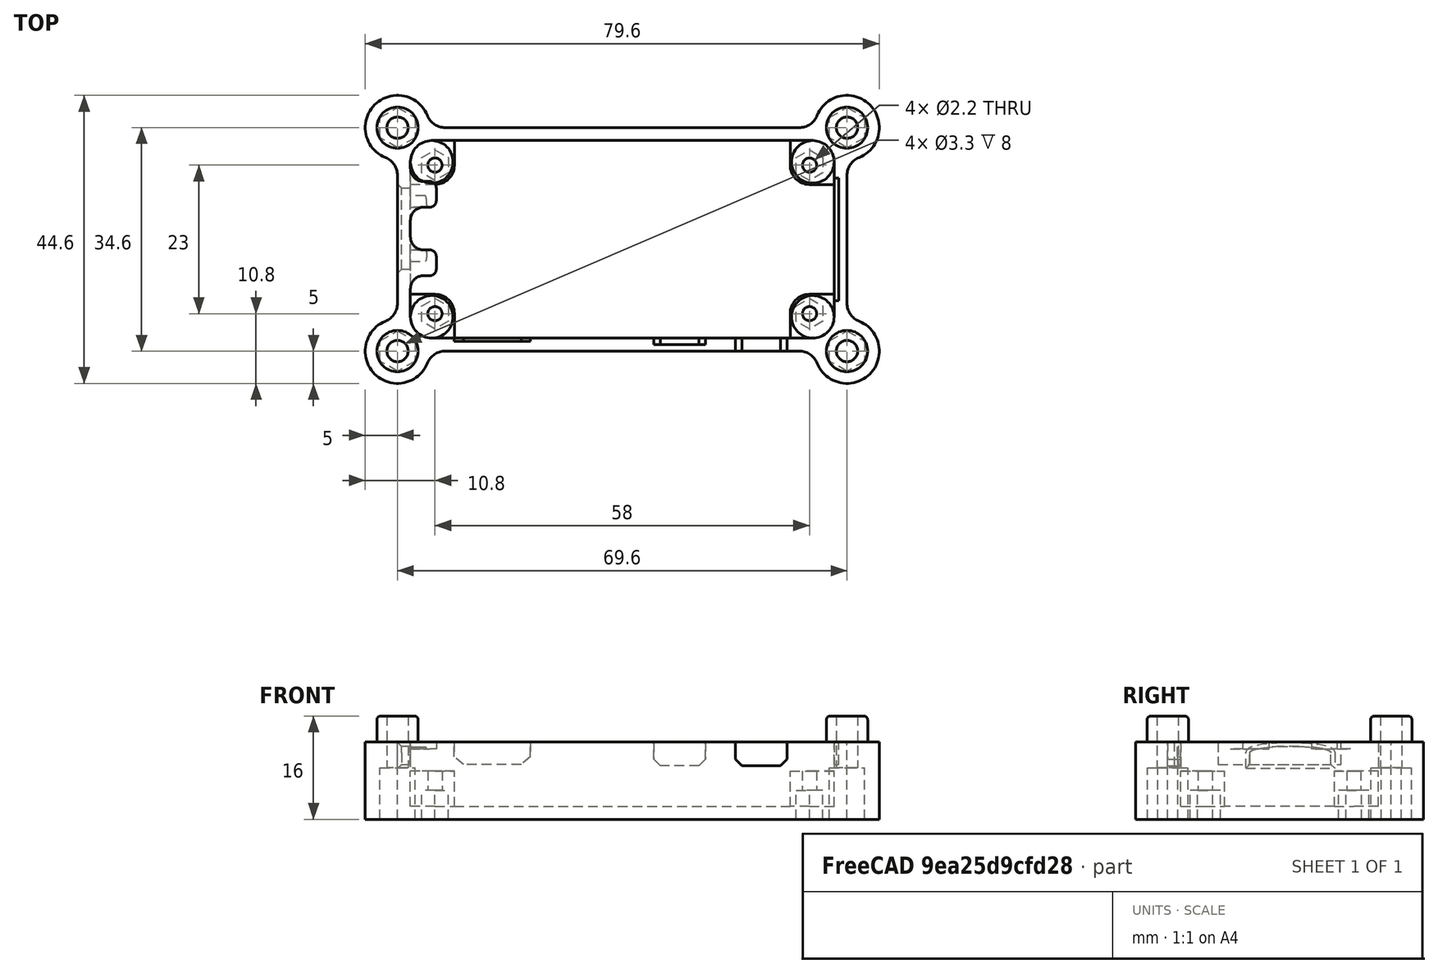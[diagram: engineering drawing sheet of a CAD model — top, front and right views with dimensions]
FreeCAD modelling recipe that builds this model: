
FCSTD DOCUMENT  (FreeCAD 0.18R14111 (Git))
Label: MMDVM_HS_Bottom-Single-USB
License: CreativeCommons Attribution-NonCommercial-ShareAlike
LicenseURL: http://creativecommons.org/licenses/by-nc-sa/4.0/
objects: Sketcher::SketchObject×16, PartDesign::Pocket×7, PartDesign::Pad×6, PartDesign::Fillet×5, PartDesign::Hole×2, PartDesign::Chamfer×1, PartDesign::Body×1, Mesh::Feature×1
note: 53 computed .brp shape members not serialized (recipe doc carries the construction recipe); baked Part::Feature solids carry a one-line shape summary decoded from their .brp

FEATURE [Sketcher::SketchObject] Sketch
  MapMode = 5
  Support = -> [XY_Plane]
  sketch-geometry (24):
    g0: LineSegment [constr] StartX=-32.5 StartY=15 StartZ=0 EndX=32.5 EndY=15 EndZ=0
    g1: LineSegment [constr] StartX=32.5 StartY=15 StartZ=0 EndX=32.5 EndY=-15 EndZ=0
    g2: LineSegment [constr] StartX=32.5 StartY=-15 StartZ=0 EndX=-32.5 EndY=-15 EndZ=0
    g3: LineSegment [constr] StartX=-32.5 StartY=-15 StartZ=0 EndX=-32.5 EndY=15 EndZ=0
    g4: LineSegment [constr] StartX=-29 StartY=11.5 StartZ=0 EndX=29 EndY=11.5 EndZ=0
    g5: LineSegment [constr] StartX=29 StartY=11.5 StartZ=0 EndX=29 EndY=-11.5 EndZ=0
    g6: LineSegment [constr] StartX=29 StartY=-11.5 StartZ=0 EndX=-29 EndY=-11.5 EndZ=0
    g7: LineSegment [constr] StartX=-29 StartY=-11.5 StartZ=0 EndX=-29 EndY=11.5 EndZ=0
    g8: Circle CenterX=-29 CenterY=11.5 CenterZ=0 NormalX=0 NormalY=0 NormalZ=1 AngleXU=0 Radius=1.375
    g9: Circle CenterX=29 CenterY=11.5 CenterZ=0 NormalX=0 NormalY=0 NormalZ=1 AngleXU=0 Radius=1.375
    g10: Circle CenterX=29 CenterY=-11.5 CenterZ=0 NormalX=0 NormalY=0 NormalZ=1 AngleXU=0 Radius=1.375
    g11: Circle CenterX=-29 CenterY=-11.5 CenterZ=0 NormalX=0 NormalY=0 NormalZ=1 AngleXU=0 Radius=1.375
    g12: LineSegment [constr] StartX=-29.5 StartY=12 StartZ=0 EndX=29.5 EndY=12 EndZ=0
    g13: LineSegment [constr] StartX=29.5 StartY=12 StartZ=0 EndX=29.5 EndY=-12 EndZ=0
    g14: LineSegment [constr] StartX=29.5 StartY=-12 StartZ=0 EndX=-29.5 EndY=-12 EndZ=0
    g15: LineSegment [constr] StartX=-29.5 StartY=-12 StartZ=0 EndX=-29.5 EndY=12 EndZ=0
    g16: ArcOfCircle CenterX=-29.5 CenterY=12 CenterZ=0 NormalX=0 NormalY=0 NormalZ=1 AngleXU=0 Radius=3 StartAngle=1.5708 EndAngle=3.1416
    g17: ArcOfCircle CenterX=29.5 CenterY=12 CenterZ=0 NormalX=0 NormalY=0 NormalZ=1 AngleXU=0 Radius=3 StartAngle=1.42077e-07 EndAngle=1.5708
    g18: ArcOfCircle CenterX=29.5 CenterY=-12 CenterZ=0 NormalX=0 NormalY=0 NormalZ=1 AngleXU=0 Radius=3 StartAngle=4.71239 EndAngle=6.28319
    g19: ArcOfCircle CenterX=-29.5 CenterY=-12 CenterZ=0 NormalX=0 NormalY=0 NormalZ=1 AngleXU=0 Radius=3 StartAngle=3.14159 EndAngle=4.71239
    g20: LineSegment StartX=-29.5 StartY=15 StartZ=0 EndX=29.5 EndY=15 EndZ=0
    g21: LineSegment StartX=32.5 StartY=12 StartZ=0 EndX=32.5 EndY=-12 EndZ=0
    g22: LineSegment StartX=29.5 StartY=-15 StartZ=0 EndX=-29.5 EndY=-15 EndZ=0
    g23: LineSegment StartX=-32.5 StartY=-12 StartZ=0 EndX=-32.5 EndY=12 EndZ=0
  constraints (68):
    c: Coincident(g0,g1)
    c: Coincident(g1,g2)
    c: Coincident(g2,g3)
    c: Coincident(g3,g0)
    c: Horizontal(g0)
    c: Horizontal(g2)
    c: Vertical(g1)
    c: Vertical(g3)
    c: DistanceX(g0,g0) = 65
    c: DistanceY(g1,g1) = 30
    c: Symmetric(g0,g0,g-2)
    c: Symmetric(g0,g1,g-1)
    c: Coincident(g4,g5)
    c: Coincident(g5,g6)
    c: Coincident(g6,g7)
    c: Coincident(g7,g4)
    c: Horizontal(g4)
    c: Horizontal(g6)
    c: Vertical(g5)
    c: Vertical(g7)
    c: DistanceX(g4,g4) = 58
    c: DistanceY(g5,g5) = 23
    c: Symmetric(g4,g5,g-1)
    c: Symmetric(g4,g4,g-2)
    c: Coincident(g8,g4)
    c: Coincident(g9,g4)
    c: Coincident(g10,g5)
    c: Coincident(g11,g6)
    c: Radius(g11) = 1.375
    c: Radius(g8) = 1.375
    c: Radius(g9) = 1.375
    c: Radius(g10) = 1.375
    c: Coincident(g12,g13)
    c: Coincident(g13,g14)
    c: Coincident(g14,g15)
    c: Coincident(g15,g12)
    c: Horizontal(g12)
    c: Horizontal(g14)
    c: Vertical(g13)
    c: Vertical(g15)
    c: DistanceX(g4,g12) = 0.5
    c: DistanceY(g4,g12) = 0.5
    c: DistanceY(g13,g5) = 0.5
    c: DistanceX(g14,g6) = 0.5
    c: Coincident(g16,g12)
    c: Radius(g16) = 3
    c: Coincident(g17,g12)
    c: Radius(g17) = 3
    c: Coincident(g18,g13)
    c: Radius(g18) = 3
    c: Coincident(g19,g14)
    c: Radius(g19) = 3
    c: PointOnObject(g16,g0)
    c: PointOnObject(g17,g1)
    c: PointOnObject(g18,g2)
    c: PointOnObject(g19,g3)
    c: Coincident(g20,g16)
    c: Horizontal(g20)
    c: Coincident(g20,g17)
    c: Coincident(g21,g17)
    c: Vertical(g21)
    c: Coincident(g18,g21)
    c: Coincident(g22,g18)
    c: Horizontal(g22)
    c: Coincident(g19,g22)
    c: Coincident(g23,g19)
    c: Vertical(g23)
    c: Coincident(g23,g16)
FEATURE [Sketcher::SketchObject] Sketch001
  MapMode = 5
  Support = -> [XY_Plane]
  expr: Constraints[8] = Sketch.Constraints[8]
  expr: Constraints[41] = Sketch.Constraints[41]
  expr: Constraints[9] = Sketch.Constraints[9]
  expr: Constraints[45] = Sketch.Constraints[45]
  expr: Constraints[43] = Sketch.Constraints[43]
  expr: Constraints[42] = Sketch.Constraints[42]
  expr: Constraints[20] = Sketch.Constraints[20]
  expr: Constraints[21] = Sketch.Constraints[21]
  expr: Constraints[28] = Sketch.Constraints[28]
  expr: Constraints[29] = Sketch.Constraints[29]
  expr: Constraints[30] = Sketch.Constraints[30]
  expr: Constraints[40] = Sketch.Constraints[40]
  expr: Constraints[31] = Sketch.Constraints[31]
  expr: Constraints[47] = Sketch.Constraints[47]
  expr: Constraints[49] = Sketch.Constraints[49]
  expr: Constraints[51] = Sketch.Constraints[51]
  sketch-geometry (64):
    g0: LineSegment [constr] StartX=-32.5 StartY=15 StartZ=0 EndX=32.5 EndY=15 EndZ=0
    g1: LineSegment [constr] StartX=32.5 StartY=15 StartZ=0 EndX=32.5 EndY=-15 EndZ=0
    g2: LineSegment [constr] StartX=32.5 StartY=-15 StartZ=0 EndX=-32.5 EndY=-15 EndZ=0
    g3: LineSegment [constr] StartX=-32.5 StartY=-15 StartZ=0 EndX=-32.5 EndY=15 EndZ=0
    g4: LineSegment [constr] StartX=-29 StartY=11.5 StartZ=0 EndX=29 EndY=11.5 EndZ=0
    g5: LineSegment [constr] StartX=29 StartY=11.5 StartZ=0 EndX=29 EndY=-11.5 EndZ=0
    g6: LineSegment [constr] StartX=29 StartY=-11.5 StartZ=0 EndX=-29 EndY=-11.5 EndZ=0
    g7: LineSegment [constr] StartX=-29 StartY=-11.5 StartZ=0 EndX=-29 EndY=11.5 EndZ=0
    g8: Circle [constr] CenterX=-29 CenterY=11.5 CenterZ=0 NormalX=0 NormalY=0 NormalZ=1 AngleXU=0 Radius=1.375
    g9: Circle [constr] CenterX=29 CenterY=11.5 CenterZ=0 NormalX=0 NormalY=0 NormalZ=1 AngleXU=0 Radius=1.375
    g10: Circle [constr] CenterX=29 CenterY=-11.5 CenterZ=0 NormalX=0 NormalY=0 NormalZ=1 AngleXU=0 Radius=1.375
    g11: Circle [constr] CenterX=-29 CenterY=-11.5 CenterZ=0 NormalX=0 NormalY=0 NormalZ=1 AngleXU=0 Radius=1.375
    g12: LineSegment [constr] StartX=-29.5 StartY=12 StartZ=0 EndX=29.5 EndY=12 EndZ=0
    g13: LineSegment [constr] StartX=29.5 StartY=12 StartZ=0 EndX=29.5 EndY=-12 EndZ=0
    g14: LineSegment [constr] StartX=29.5 StartY=-12 StartZ=0 EndX=-29.5 EndY=-12 EndZ=0
    g15: LineSegment [constr] StartX=-29.5 StartY=-12 StartZ=0 EndX=-29.5 EndY=12 EndZ=0
    g16: ArcOfCircle [constr] CenterX=-29.5 CenterY=12 CenterZ=0 NormalX=0 NormalY=0 NormalZ=1 AngleXU=0 Radius=3 StartAngle=1.5708 EndAngle=3.14159
    g17: ArcOfCircle [constr] CenterX=29.5 CenterY=12 CenterZ=0 NormalX=0 NormalY=0 NormalZ=1 AngleXU=0 Radius=3 StartAngle=2.8425e-08 EndAngle=1.5708
    g18: ArcOfCircle [constr] CenterX=29.5 CenterY=-12 CenterZ=0 NormalX=0 NormalY=0 NormalZ=1 AngleXU=0 Radius=3 StartAngle=4.71239 EndAngle=6.28319
    g19: ArcOfCircle [constr] CenterX=-29.5 CenterY=-12 CenterZ=0 NormalX=0 NormalY=0 NormalZ=1 AngleXU=0 Radius=3 StartAngle=3.14159 EndAngle=4.71239
    g20: LineSegment [constr] StartX=-29.5 StartY=15 StartZ=0 EndX=29.5 EndY=15 EndZ=0
    g21: LineSegment [constr] StartX=32.5 StartY=12 StartZ=0 EndX=32.5 EndY=-12 EndZ=0
    g22: LineSegment [constr] StartX=29.5 StartY=-15 StartZ=0 EndX=-29.5 EndY=-15 EndZ=0
    g23: LineSegment [constr] StartX=-32.5 StartY=-12 StartZ=0 EndX=-32.5 EndY=12 EndZ=0
    g24: ArcOfCircle [constr] CenterX=-29.5 CenterY=12 CenterZ=0 NormalX=0 NormalY=0 NormalZ=1 AngleXU=0 Radius=3.3 StartAngle=1.5708 EndAngle=3.14159
    g25: ArcOfCircle [constr] CenterX=29.5 CenterY=12 CenterZ=0 NormalX=0 NormalY=0 NormalZ=1 AngleXU=0 Radius=3.3 StartAngle=-2.2e-10 EndAngle=1.5708
    g26: ArcOfCircle [constr] CenterX=29.5 CenterY=-12 CenterZ=0 NormalX=0 NormalY=0 NormalZ=1 AngleXU=0 Radius=3.3 StartAngle=4.71239 EndAngle=6.28319
    g27: ArcOfCircle [constr] CenterX=-29.5 CenterY=-12 CenterZ=0 NormalX=0 NormalY=0 NormalZ=1 AngleXU=0 Radius=3.3 StartAngle=3.14159 EndAngle=4.71239
    g28: LineSegment [constr] StartX=-32.8 StartY=12 StartZ=0 EndX=-32.8 EndY=-12 EndZ=0
    g29: LineSegment [constr] StartX=-29.5 StartY=15.3 StartZ=0 EndX=29.5 EndY=15.3 EndZ=0
    g30: LineSegment [constr] StartX=32.8 StartY=12 StartZ=0 EndX=32.8 EndY=-12 EndZ=0
    g31: LineSegment [constr] StartX=29.5 StartY=-15.3 StartZ=0 EndX=-29.5 EndY=-15.3 EndZ=0
    g32: LineSegment [constr] StartX=-34.8 StartY=17.3 StartZ=0 EndX=34.8 EndY=17.3 EndZ=0
    g33: LineSegment [constr] StartX=34.8 StartY=17.3 StartZ=0 EndX=34.8 EndY=-17.3 EndZ=0
    g34: LineSegment [constr] StartX=34.8 StartY=-17.3 StartZ=0 EndX=-34.8 EndY=-17.3 EndZ=0
    g35: LineSegment [constr] StartX=-34.8 StartY=-17.3 StartZ=0 EndX=-34.8 EndY=17.3 EndZ=0
    g36: Circle [constr] CenterX=34.8 CenterY=17.3 CenterZ=0 NormalX=0 NormalY=0 NormalZ=1 AngleXU=0 Radius=5
    g37: Circle [constr] CenterX=34.8 CenterY=-17.3 CenterZ=0 NormalX=0 NormalY=0 NormalZ=1 AngleXU=0 Radius=5
    g38: Circle [constr] CenterX=-34.8 CenterY=-17.3 CenterZ=0 NormalX=0 NormalY=0 NormalZ=1 AngleXU=0 Radius=5
    g39: Circle [constr] CenterX=-34.8 CenterY=17.3 CenterZ=0 NormalX=0 NormalY=0 NormalZ=1 AngleXU=0 Radius=5
    g40: Circle [constr] CenterX=27.3838 CenterY=20.3 CenterZ=0 NormalX=0 NormalY=0 NormalZ=1 AngleXU=0 Radius=3
    g41: Circle [constr] CenterX=-27.3838 CenterY=20.3 CenterZ=0 NormalX=0 NormalY=0 NormalZ=1 AngleXU=0 Radius=3
    g42: Circle [constr] CenterX=-37.8 CenterY=9.8838 CenterZ=0 NormalX=0 NormalY=0 NormalZ=1 AngleXU=0 Radius=3
    g43: Circle [constr] CenterX=-37.8 CenterY=-9.8838 CenterZ=0 NormalX=0 NormalY=0 NormalZ=1 AngleXU=0 Radius=3
    g44: Circle [constr] CenterX=-27.3838 CenterY=-20.3 CenterZ=0 NormalX=0 NormalY=0 NormalZ=1 AngleXU=0 Radius=3
    g45: Circle [constr] CenterX=27.3838 CenterY=-20.3 CenterZ=0 NormalX=0 NormalY=0 NormalZ=1 AngleXU=0 Radius=3
    g46: Circle [constr] CenterX=37.8 CenterY=-9.8838 CenterZ=0 NormalX=0 NormalY=0 NormalZ=1 AngleXU=0 Radius=3
    g47: Circle [constr] CenterX=37.8 CenterY=9.8838 CenterZ=0 NormalX=0 NormalY=0 NormalZ=1 AngleXU=0 Radius=3
    g48: ArcOfCircle CenterX=34.8 CenterY=17.3 CenterZ=0 NormalX=0 NormalY=0 NormalZ=1 AngleXU=0 Radius=5 StartAngle=5.09679 EndAngle=9.04038
    g49: ArcOfCircle CenterX=27.3838 CenterY=20.3 CenterZ=0 NormalX=0 NormalY=0 NormalZ=1 AngleXU=0 Radius=3 StartAngle=4.71239 EndAngle=5.89879
    g50: ArcOfCircle CenterX=37.8 CenterY=9.8838 CenterZ=0 NormalX=0 NormalY=0 NormalZ=1 AngleXU=0 Radius=3 StartAngle=1.95519 EndAngle=3.14159
    g51: ArcOfCircle CenterX=37.8 CenterY=-9.8838 CenterZ=0 NormalX=0 NormalY=0 NormalZ=1 AngleXU=0 Radius=3 StartAngle=3.14159 EndAngle=4.32799
    g52: ArcOfCircle CenterX=34.8 CenterY=-17.3 CenterZ=0 NormalX=0 NormalY=0 NormalZ=1 AngleXU=0 Radius=5 StartAngle=3.52599 EndAngle=7.46958
    g53: ArcOfCircle CenterX=27.3838 CenterY=-20.3 CenterZ=0 NormalX=0 NormalY=0 NormalZ=1 AngleXU=0 Radius=3 StartAngle=0.384397 EndAngle=1.5708
    g54: ArcOfCircle CenterX=-27.3838 CenterY=-20.3 CenterZ=0 NormalX=0 NormalY=0 NormalZ=1 AngleXU=0 Radius=3 StartAngle=1.5708 EndAngle=2.7572
    g55: ArcOfCircle CenterX=-34.8 CenterY=-17.3 CenterZ=0 NormalX=0 NormalY=0 NormalZ=1 AngleXU=0 Radius=5 StartAngle=1.95519 EndAngle=5.89879
    g56: ArcOfCircle CenterX=-37.8 CenterY=-9.8838 CenterZ=0 NormalX=0 NormalY=0 NormalZ=1 AngleXU=0 Radius=3 StartAngle=5.09679 EndAngle=6.28319
    g57: ArcOfCircle CenterX=-37.8 CenterY=9.8838 CenterZ=0 NormalX=0 NormalY=0 NormalZ=1 AngleXU=0 Radius=3 StartAngle=6.28319 EndAngle=7.46958
    g58: ArcOfCircle CenterX=-34.8 CenterY=17.3 CenterZ=0 NormalX=0 NormalY=0 NormalZ=1 AngleXU=0 Radius=5 StartAngle=0.384397 EndAngle=4.32799
    g59: ArcOfCircle CenterX=-27.3838 CenterY=20.3 CenterZ=0 NormalX=0 NormalY=0 NormalZ=1 AngleXU=0 Radius=3 StartAngle=3.52599 EndAngle=4.71239
    g60: LineSegment StartX=-27.3838 StartY=17.3 StartZ=0 EndX=27.3838 EndY=17.3 EndZ=0
    g61: LineSegment StartX=34.8 StartY=9.8838 StartZ=0 EndX=34.8 EndY=-9.8838 EndZ=0
    g62: LineSegment StartX=27.3838 StartY=-17.3 StartZ=0 EndX=-27.3838 EndY=-17.3 EndZ=0
    g63: LineSegment StartX=-34.8 StartY=-9.8838 StartZ=0 EndX=-34.8 EndY=9.8838 EndZ=0
  constraints (184):
    c: Coincident(g0,g1)
    c: Coincident(g1,g2)
    c: Coincident(g2,g3)
    c: Coincident(g3,g0)
    c: Horizontal(g0)
    c: Horizontal(g2)
    c: Vertical(g1)
    c: Vertical(g3)
    c: DistanceX(g0,g0) = 65
    c: DistanceY(g1,g1) = 30
    c: Symmetric(g0,g0,g-2)
    c: Symmetric(g0,g1,g-1)
    c: Coincident(g4,g5)
    c: Coincident(g5,g6)
    c: Coincident(g6,g7)
    c: Coincident(g7,g4)
    c: Horizontal(g4)
    c: Horizontal(g6)
    c: Vertical(g5)
    c: Vertical(g7)
    c: DistanceX(g4,g4) = 58
    c: DistanceY(g5,g5) = 23
    c: Symmetric(g4,g5,g-1)
    c: Symmetric(g4,g4,g-2)
    c: Coincident(g8,g4)
    c: Coincident(g9,g4)
    c: Coincident(g10,g5)
    c: Coincident(g11,g6)
    c: Radius(g11) = 1.375
    c: Radius(g8) = 1.375
    c: Radius(g9) = 1.375
    c: Radius(g10) = 1.375
    c: Coincident(g12,g13)
    c: Coincident(g13,g14)
    c: Coincident(g14,g15)
    c: Coincident(g15,g12)
    c: Horizontal(g12)
    c: Horizontal(g14)
    c: Vertical(g13)
    c: Vertical(g15)
    c: DistanceX(g4,g12) = 0.5
    c: DistanceY(g4,g12) = 0.5
    c: DistanceY(g13,g5) = 0.5
    c: DistanceX(g14,g6) = 0.5
    c: Coincident(g16,g12)
    c: Radius(g16) = 3
    c: Coincident(g17,g12)
    c: Radius(g17) = 3
    c: Coincident(g18,g13)
    c: Radius(g18) = 3
    c: Coincident(g19,g14)
    c: Radius(g19) = 3
    c: PointOnObject(g16,g0)
    c: PointOnObject(g17,g1)
    c: PointOnObject(g18,g2)
    c: PointOnObject(g19,g3)
    c: Coincident(g20,g16)
    c: Horizontal(g20)
    c: Coincident(g20,g17)
    c: Coincident(g21,g17)
    c: Vertical(g21)
    c: Coincident(g18,g21)
    c: Coincident(g22,g18)
    c: Horizontal(g22)
    c: Coincident(g19,g22)
    c: Coincident(g23,g19)
    c: Vertical(g23)
    c: Coincident(g23,g16)
    c: Coincident(g24,g12)
    c: Radius(g24) = 3.3
    c: Coincident(g25,g12)
    c: Radius(g25) = 3.3
    c: Coincident(g26,g13)
    c: Radius(g26) = 3.3
    c: Coincident(g27,g14)
    c: Radius(g27) = 3.3
    c: Vertical(g28)
    c: DistanceX(g28,g2) = 0.3
    c: Coincident(g27,g28)
    c: Coincident(g28,g24)
    c: Horizontal(g29)
    c: DistanceY(g0,g29) = 0.3
    c: Coincident(g24,g29)
    c: Coincident(g25,g29)
    c: Vertical(g30)
    c: DistanceX(g0,g30) = 0.3
    c: Coincident(g25,g30)
    c: Coincident(g30,g26)
    c: Horizontal(g31)
    c: DistanceY(g31,g1) = 0.3
    c: Coincident(g31,g26)
    c: Coincident(g31,g27)
    c: Coincident(g32,g33)
    c: Coincident(g33,g34)
    c: Coincident(g34,g35)
    c: Coincident(g35,g32)
    c: Horizontal(g32)
    c: Horizontal(g34)
    c: Vertical(g33)
    c: Vertical(g35)
    c: DistanceY(g25,g32) = 2
    c: DistanceX(g25,g32) = 2
    c: DistanceY(g33,g26) = 2
    c: DistanceX(g34,g27) = 2
    c: Coincident(g36,g32)
    c: Coincident(g37,g33)
    c: Coincident(g38,g34)
    c: Coincident(g39,g32)
    c: Radius(g39) = 5
    c: Radius(g38) = 5
    c: Radius(g37) = 5
    c: Radius(g36) = 5
    c: Radius(g40) = 3
    c: Tangent(g40,g36)
    c: Tangent(g40,g32)
    c: Tangent(g47,g36)
    c: Radius(g47) = 3
    c: Tangent(g47,g33)
    c: Radius(g46) = 3
    c: Tangent(g46,g37)
    c: Tangent(g46,g33)
    c: Radius(g45) = 3
    c: Tangent(g45,g37)
    c: Tangent(g45,g34)
    c: Radius(g44) = 3
    c: Tangent(g44,g34)
    c: Tangent(g44,g38)
    c: Radius(g43) = 3
    c: Tangent(g43,g38)
    c: Tangent(g43,g35)
    c: Radius(g42) = 3
    c: Tangent(g42,g35)
    c: Tangent(g42,g39)
    c: Radius(g41) = 3
    c: Tangent(g41,g32)
    c: Tangent(g41,g39)
    c: Coincident(g48,g32)
    c: PointOnObject(g48,g36)
    c: Coincident(g49,g40)
    c: PointOnObject(g49,g40)
    c: Coincident(g50,g47)
    c: PointOnObject(g50,g47)
    c: Coincident(g51,g46)
    c: PointOnObject(g51,g46)
    c: Coincident(g52,g33)
    c: PointOnObject(g52,g37)
    c: Coincident(g53,g45)
    c: PointOnObject(g53,g45)
    c: Coincident(g54,g44)
    c: PointOnObject(g54,g44)
    c: Coincident(g55,g34)
    c: PointOnObject(g55,g38)
    c: Coincident(g56,g43)
    c: PointOnObject(g56,g43)
    c: Coincident(g57,g42)
    c: PointOnObject(g57,g42)
    c: Coincident(g58,g32)
    c: PointOnObject(g58,g39)
    c: Coincident(g59,g41)
    c: PointOnObject(g59,g41)
    c: Coincident(g49,g48)
    c: Coincident(g48,g50)
    c: Coincident(g51,g52)
    c: Coincident(g52,g53)
    c: Coincident(g54,g55)
    c: Coincident(g55,g56)
    c: Coincident(g57,g58)
    c: Coincident(g58,g59)
    c: PointOnObject(g60,g32)
    c: Horizontal(g60)
    c: PointOnObject(g61,g33)
    c: Vertical(g61)
    c: PointOnObject(g62,g34)
    c: Horizontal(g62)
    c: PointOnObject(g63,g35)
    c: Vertical(g63)
    c: Coincident(g59,g60)
    c: Coincident(g60,g49)
    c: Coincident(g50,g61)
    c: Coincident(g61,g51)
    c: Coincident(g53,g62)
    c: Coincident(g54,g62)
    c: Coincident(g56,g63)
    c: Coincident(g57,g63)
FEATURE [PartDesign::Pad] Pad
  Length = 12
  Length2 = 100
  Profile = -> Sketch001
  Type = 0
FEATURE [Sketcher::SketchObject] Sketch002
  MapMode = 5
  Placement = pos=(0,0,12) rot=(0,0,1;0rad)
  Support = -> [Pad]
  expr: Constraints[133] = Sketch001.Constraints[133]
  expr: Constraints[130] = Sketch001.Constraints[130]
  expr: Constraints[112] = Sketch001.Constraints[112]
  expr: Constraints[124] = Sketch001.Constraints[124]
  expr: Constraints[127] = Sketch001.Constraints[127]
  expr: Constraints[110] = Sketch001.Constraints[110]
  expr: Constraints[51] = Sketch001.Constraints[51]
  expr: Constraints[100] = Sketch001.Constraints[100]
  expr: Constraints[77] = Sketch001.Constraints[77]
  expr: Constraints[89] = Sketch001.Constraints[89]
  expr: Constraints[85] = Sketch001.Constraints[85]
  expr: Constraints[118] = Sketch001.Constraints[118]
  expr: Constraints[71] = Sketch001.Constraints[71]
  expr: Constraints[111] = Sketch001.Constraints[111]
  expr: Constraints[103] = Sketch001.Constraints[103]
  expr: Constraints[49] = Sketch001.Constraints[49]
  expr: Constraints[102] = Sketch001.Constraints[102]
  expr: Constraints[69] = Sketch001.Constraints[69]
  expr: Constraints[47] = Sketch001.Constraints[47]
  expr: Constraints[73] = Sketch001.Constraints[73]
  expr: Constraints[75] = Sketch001.Constraints[75]
  expr: Constraints[31] = Sketch001.Constraints[31]
  expr: Constraints[116] = Sketch001.Constraints[116]
  expr: Constraints[40] = Sketch001.Constraints[40]
  expr: Constraints[30] = Sketch001.Constraints[30]
  expr: Constraints[29] = Sketch001.Constraints[29]
  expr: Constraints[28] = Sketch001.Constraints[28]
  expr: Constraints[121] = Sketch001.Constraints[121]
  expr: Constraints[21] = Sketch001.Constraints[21]
  expr: Constraints[20] = Sketch001.Constraints[20]
  expr: Constraints[42] = Sketch001.Constraints[42]
  expr: Constraints[43] = Sketch001.Constraints[43]
  expr: Constraints[101] = Sketch001.Constraints[101]
  expr: Constraints[45] = Sketch001.Constraints[45]
  expr: Constraints[108] = Sketch001.Constraints[108]
  expr: Constraints[41] = Sketch001.Constraints[41]
  expr: Constraints[9] = Sketch001.Constraints[9]
  expr: Constraints[81] = Sketch001.Constraints[81]
  expr: Constraints[109] = Sketch001.Constraints[109]
  expr: Constraints[8] = Sketch001.Constraints[8]
  sketch-geometry (64):
    g0: LineSegment [constr] StartX=-32.5 StartY=15 StartZ=0 EndX=32.5 EndY=15 EndZ=0
    g1: LineSegment [constr] StartX=32.5 StartY=15 StartZ=0 EndX=32.5 EndY=-15 EndZ=0
    g2: LineSegment [constr] StartX=32.5 StartY=-15 StartZ=0 EndX=-32.5 EndY=-15 EndZ=0
    g3: LineSegment [constr] StartX=-32.5 StartY=-15 StartZ=0 EndX=-32.5 EndY=15 EndZ=0
    g4: LineSegment [constr] StartX=-29 StartY=11.5 StartZ=0 EndX=29 EndY=11.5 EndZ=0
    g5: LineSegment [constr] StartX=29 StartY=11.5 StartZ=0 EndX=29 EndY=-11.5 EndZ=0
    g6: LineSegment [constr] StartX=29 StartY=-11.5 StartZ=0 EndX=-29 EndY=-11.5 EndZ=0
    g7: LineSegment [constr] StartX=-29 StartY=-11.5 StartZ=0 EndX=-29 EndY=11.5 EndZ=0
    g8: Circle [constr] CenterX=-29 CenterY=11.5 CenterZ=0 NormalX=0 NormalY=0 NormalZ=1 AngleXU=0 Radius=1.375
    g9: Circle [constr] CenterX=29 CenterY=11.5 CenterZ=0 NormalX=0 NormalY=0 NormalZ=1 AngleXU=0 Radius=1.375
    g10: Circle [constr] CenterX=29 CenterY=-11.5 CenterZ=0 NormalX=0 NormalY=0 NormalZ=1 AngleXU=0 Radius=1.375
    g11: Circle [constr] CenterX=-29 CenterY=-11.5 CenterZ=0 NormalX=0 NormalY=0 NormalZ=1 AngleXU=0 Radius=1.375
    g12: LineSegment [constr] StartX=-29.5 StartY=12 StartZ=0 EndX=29.5 EndY=12 EndZ=0
    g13: LineSegment [constr] StartX=29.5 StartY=12 StartZ=0 EndX=29.5 EndY=-12 EndZ=0
    g14: LineSegment [constr] StartX=29.5 StartY=-12 StartZ=0 EndX=-29.5 EndY=-12 EndZ=0
    g15: LineSegment [constr] StartX=-29.5 StartY=-12 StartZ=0 EndX=-29.5 EndY=12 EndZ=0
    g16: ArcOfCircle [constr] CenterX=-29.5 CenterY=12 CenterZ=0 NormalX=0 NormalY=0 NormalZ=1 AngleXU=0 Radius=3 StartAngle=1.5708 EndAngle=3.14159
    g17: ArcOfCircle [constr] CenterX=29.5 CenterY=12 CenterZ=0 NormalX=0 NormalY=0 NormalZ=1 AngleXU=0 Radius=3 StartAngle=2.8425e-08 EndAngle=1.5708
    g18: ArcOfCircle [constr] CenterX=29.5 CenterY=-12 CenterZ=0 NormalX=0 NormalY=0 NormalZ=1 AngleXU=0 Radius=3 StartAngle=4.71239 EndAngle=6.28319
    g19: ArcOfCircle [constr] CenterX=-29.5 CenterY=-12 CenterZ=0 NormalX=0 NormalY=0 NormalZ=1 AngleXU=0 Radius=3 StartAngle=3.14159 EndAngle=4.71239
    g20: LineSegment [constr] StartX=-29.5 StartY=15 StartZ=0 EndX=29.5 EndY=15 EndZ=0
    g21: LineSegment [constr] StartX=32.5 StartY=12 StartZ=0 EndX=32.5 EndY=-12 EndZ=0
    g22: LineSegment [constr] StartX=29.5 StartY=-15 StartZ=0 EndX=-29.5 EndY=-15 EndZ=0
    g23: LineSegment [constr] StartX=-32.5 StartY=-12 StartZ=0 EndX=-32.5 EndY=12 EndZ=0
    g24: ArcOfCircle CenterX=-29.5 CenterY=12 CenterZ=0 NormalX=0 NormalY=0 NormalZ=1 AngleXU=0 Radius=3.3 StartAngle=1.5708 EndAngle=3.14159
    g25: ArcOfCircle CenterX=29.5 CenterY=12 CenterZ=0 NormalX=0 NormalY=0 NormalZ=1 AngleXU=0 Radius=3.3 StartAngle=-2.2e-10 EndAngle=1.5708
    g26: ArcOfCircle CenterX=29.5 CenterY=-12 CenterZ=0 NormalX=0 NormalY=0 NormalZ=1 AngleXU=0 Radius=3.3 StartAngle=4.71239 EndAngle=6.28319
    g27: ArcOfCircle CenterX=-29.5 CenterY=-12 CenterZ=0 NormalX=0 NormalY=0 NormalZ=1 AngleXU=0 Radius=3.3 StartAngle=3.14159 EndAngle=4.71239
    g28: LineSegment StartX=-32.8 StartY=12 StartZ=0 EndX=-32.8 EndY=-12 EndZ=0
    g29: LineSegment StartX=-29.5 StartY=15.3 StartZ=0 EndX=29.5 EndY=15.3 EndZ=0
    g30: LineSegment StartX=32.8 StartY=12 StartZ=0 EndX=32.8 EndY=-12 EndZ=0
    g31: LineSegment StartX=29.5 StartY=-15.3 StartZ=0 EndX=-29.5 EndY=-15.3 EndZ=0
    g32: LineSegment [constr] StartX=-34.8 StartY=17.3 StartZ=0 EndX=34.8 EndY=17.3 EndZ=0
    g33: LineSegment [constr] StartX=34.8 StartY=17.3 StartZ=0 EndX=34.8 EndY=-17.3 EndZ=0
    g34: LineSegment [constr] StartX=34.8 StartY=-17.3 StartZ=0 EndX=-34.8 EndY=-17.3 EndZ=0
    g35: LineSegment [constr] StartX=-34.8 StartY=-17.3 StartZ=0 EndX=-34.8 EndY=17.3 EndZ=0
    g36: Circle [constr] CenterX=34.8 CenterY=17.3 CenterZ=0 NormalX=0 NormalY=0 NormalZ=1 AngleXU=0 Radius=5
    g37: Circle [constr] CenterX=34.8 CenterY=-17.3 CenterZ=0 NormalX=0 NormalY=0 NormalZ=1 AngleXU=0 Radius=5
    g38: Circle [constr] CenterX=-34.8 CenterY=-17.3 CenterZ=0 NormalX=0 NormalY=0 NormalZ=1 AngleXU=0 Radius=5
    g39: Circle [constr] CenterX=-34.8 CenterY=17.3 CenterZ=0 NormalX=0 NormalY=0 NormalZ=1 AngleXU=0 Radius=5
    g40: Circle [constr] CenterX=27.3838 CenterY=20.3 CenterZ=0 NormalX=0 NormalY=0 NormalZ=1 AngleXU=0 Radius=3
    g41: Circle [constr] CenterX=-27.3838 CenterY=20.3 CenterZ=0 NormalX=0 NormalY=0 NormalZ=1 AngleXU=0 Radius=3
    g42: Circle [constr] CenterX=-37.8 CenterY=9.8838 CenterZ=0 NormalX=0 NormalY=0 NormalZ=1 AngleXU=0 Radius=3
    g43: Circle [constr] CenterX=-37.8 CenterY=-9.8838 CenterZ=0 NormalX=0 NormalY=0 NormalZ=1 AngleXU=0 Radius=3
    g44: Circle [constr] CenterX=-27.3838 CenterY=-20.3 CenterZ=0 NormalX=0 NormalY=0 NormalZ=1 AngleXU=0 Radius=3
    g45: Circle [constr] CenterX=27.3838 CenterY=-20.3 CenterZ=0 NormalX=0 NormalY=0 NormalZ=1 AngleXU=0 Radius=3
    g46: Circle [constr] CenterX=37.8 CenterY=-9.8838 CenterZ=0 NormalX=0 NormalY=0 NormalZ=1 AngleXU=0 Radius=3
    g47: Circle [constr] CenterX=37.8 CenterY=9.8838 CenterZ=0 NormalX=0 NormalY=0 NormalZ=1 AngleXU=0 Radius=3
    g48: ArcOfCircle [constr] CenterX=34.8 CenterY=17.3 CenterZ=0 NormalX=0 NormalY=0 NormalZ=1 AngleXU=0 Radius=5 StartAngle=5.09679 EndAngle=9.04038
    g49: ArcOfCircle [constr] CenterX=27.3838 CenterY=20.3 CenterZ=0 NormalX=0 NormalY=0 NormalZ=1 AngleXU=0 Radius=3 StartAngle=4.71239 EndAngle=5.89879
    g50: ArcOfCircle [constr] CenterX=37.8 CenterY=9.8838 CenterZ=0 NormalX=0 NormalY=0 NormalZ=1 AngleXU=0 Radius=3 StartAngle=1.95519 EndAngle=3.14159
    g51: ArcOfCircle [constr] CenterX=37.8 CenterY=-9.8838 CenterZ=0 NormalX=0 NormalY=0 NormalZ=1 AngleXU=0 Radius=3 StartAngle=3.14159 EndAngle=4.32799
    g52: ArcOfCircle [constr] CenterX=34.8 CenterY=-17.3 CenterZ=0 NormalX=0 NormalY=0 NormalZ=1 AngleXU=0 Radius=5 StartAngle=3.52599 EndAngle=7.46958
    g53: ArcOfCircle [constr] CenterX=27.3838 CenterY=-20.3 CenterZ=0 NormalX=0 NormalY=0 NormalZ=1 AngleXU=0 Radius=3 StartAngle=0.384397 EndAngle=1.5708
    g54: ArcOfCircle [constr] CenterX=-27.3838 CenterY=-20.3 CenterZ=0 NormalX=0 NormalY=0 NormalZ=1 AngleXU=0 Radius=3 StartAngle=1.5708 EndAngle=2.7572
    g55: ArcOfCircle [constr] CenterX=-34.8 CenterY=-17.3 CenterZ=0 NormalX=0 NormalY=0 NormalZ=1 AngleXU=0 Radius=5 StartAngle=1.95519 EndAngle=5.89879
    g56: ArcOfCircle [constr] CenterX=-37.8 CenterY=-9.8838 CenterZ=0 NormalX=0 NormalY=0 NormalZ=1 AngleXU=0 Radius=3 StartAngle=5.09679 EndAngle=6.28319
    g57: ArcOfCircle [constr] CenterX=-37.8 CenterY=9.8838 CenterZ=0 NormalX=0 NormalY=0 NormalZ=1 AngleXU=0 Radius=3 StartAngle=6.28319 EndAngle=7.46958
    g58: ArcOfCircle [constr] CenterX=-34.8 CenterY=17.3 CenterZ=0 NormalX=0 NormalY=0 NormalZ=1 AngleXU=0 Radius=5 StartAngle=0.384397 EndAngle=4.32799
    g59: ArcOfCircle [constr] CenterX=-27.3838 CenterY=20.3 CenterZ=0 NormalX=0 NormalY=0 NormalZ=1 AngleXU=0 Radius=3 StartAngle=3.52599 EndAngle=4.71239
    g60: LineSegment [constr] StartX=-27.3838 StartY=17.3 StartZ=0 EndX=27.3838 EndY=17.3 EndZ=0
    g61: LineSegment [constr] StartX=34.8 StartY=9.8838 StartZ=0 EndX=34.8 EndY=-9.8838 EndZ=0
    g62: LineSegment [constr] StartX=27.3838 StartY=-17.3 StartZ=0 EndX=-27.3838 EndY=-17.3 EndZ=0
    g63: LineSegment [constr] StartX=-34.8 StartY=-9.8838 StartZ=0 EndX=-34.8 EndY=9.8838 EndZ=0
  constraints (184):
    c: Coincident(g0,g1)
    c: Coincident(g1,g2)
    c: Coincident(g2,g3)
    c: Coincident(g3,g0)
    c: Horizontal(g0)
    c: Horizontal(g2)
    c: Vertical(g1)
    c: Vertical(g3)
    c: DistanceX(g0,g0) = 65
    c: DistanceY(g1,g1) = 30
    c: Symmetric(g0,g0,g-2)
    c: Symmetric(g0,g1,g-1)
    c: Coincident(g4,g5)
    c: Coincident(g5,g6)
    c: Coincident(g6,g7)
    c: Coincident(g7,g4)
    c: Horizontal(g4)
    c: Horizontal(g6)
    c: Vertical(g5)
    c: Vertical(g7)
    c: DistanceX(g4,g4) = 58
    c: DistanceY(g5,g5) = 23
    c: Symmetric(g4,g5,g-1)
    c: Symmetric(g4,g4,g-2)
    c: Coincident(g8,g4)
    c: Coincident(g9,g4)
    c: Coincident(g10,g5)
    c: Coincident(g11,g6)
    c: Radius(g11) = 1.375
    c: Radius(g8) = 1.375
    c: Radius(g9) = 1.375
    c: Radius(g10) = 1.375
    c: Coincident(g12,g13)
    c: Coincident(g13,g14)
    c: Coincident(g14,g15)
    c: Coincident(g15,g12)
    c: Horizontal(g12)
    c: Horizontal(g14)
    c: Vertical(g13)
    c: Vertical(g15)
    c: DistanceX(g4,g12) = 0.5
    c: DistanceY(g4,g12) = 0.5
    c: DistanceY(g13,g5) = 0.5
    c: DistanceX(g14,g6) = 0.5
    c: Coincident(g16,g12)
    c: Radius(g16) = 3
    c: Coincident(g17,g12)
    c: Radius(g17) = 3
    c: Coincident(g18,g13)
    c: Radius(g18) = 3
    c: Coincident(g19,g14)
    c: Radius(g19) = 3
    c: PointOnObject(g16,g0)
    c: PointOnObject(g17,g1)
    c: PointOnObject(g18,g2)
    c: PointOnObject(g19,g3)
    c: Coincident(g20,g16)
    c: Horizontal(g20)
    c: Coincident(g20,g17)
    c: Coincident(g21,g17)
    c: Vertical(g21)
    c: Coincident(g18,g21)
    c: Coincident(g22,g18)
    c: Horizontal(g22)
    c: Coincident(g19,g22)
    c: Coincident(g23,g19)
    c: Vertical(g23)
    c: Coincident(g23,g16)
    c: Coincident(g24,g12)
    c: Radius(g24) = 3.3
    c: Coincident(g25,g12)
    c: Radius(g25) = 3.3
    c: Coincident(g26,g13)
    c: Radius(g26) = 3.3
    c: Coincident(g27,g14)
    c: Radius(g27) = 3.3
    c: Vertical(g28)
    c: DistanceX(g28,g2) = 0.3
    c: Coincident(g27,g28)
    c: Coincident(g28,g24)
    c: Horizontal(g29)
    c: DistanceY(g0,g29) = 0.3
    c: Coincident(g24,g29)
    c: Coincident(g25,g29)
    c: Vertical(g30)
    c: DistanceX(g0,g30) = 0.3
    c: Coincident(g25,g30)
    c: Coincident(g30,g26)
    c: Horizontal(g31)
    c: DistanceY(g31,g1) = 0.3
    c: Coincident(g31,g26)
    c: Coincident(g31,g27)
    c: Coincident(g32,g33)
    c: Coincident(g33,g34)
    c: Coincident(g34,g35)
    c: Coincident(g35,g32)
    c: Horizontal(g32)
    c: Horizontal(g34)
    c: Vertical(g33)
    c: Vertical(g35)
    c: DistanceY(g25,g32) = 2
    c: DistanceX(g25,g32) = 2
    c: DistanceY(g33,g26) = 2
    c: DistanceX(g34,g27) = 2
    c: Coincident(g36,g32)
    c: Coincident(g37,g33)
    c: Coincident(g38,g34)
    c: Coincident(g39,g32)
    c: Radius(g39) = 5
    c: Radius(g38) = 5
    c: Radius(g37) = 5
    c: Radius(g36) = 5
    c: Radius(g40) = 3
    c: Tangent(g40,g36)
    c: Tangent(g40,g32)
    c: Tangent(g47,g36)
    c: Radius(g47) = 3
    c: Tangent(g47,g33)
    c: Radius(g46) = 3
    c: Tangent(g46,g37)
    c: Tangent(g46,g33)
    c: Radius(g45) = 3
    c: Tangent(g45,g37)
    c: Tangent(g45,g34)
    c: Radius(g44) = 3
    c: Tangent(g44,g34)
    c: Tangent(g44,g38)
    c: Radius(g43) = 3
    c: Tangent(g43,g38)
    c: Tangent(g43,g35)
    c: Radius(g42) = 3
    c: Tangent(g42,g35)
    c: Tangent(g42,g39)
    c: Radius(g41) = 3
    c: Tangent(g41,g32)
    c: Tangent(g41,g39)
    c: Coincident(g48,g32)
    c: PointOnObject(g48,g36)
    c: Coincident(g49,g40)
    c: PointOnObject(g49,g40)
    c: Coincident(g50,g47)
    c: PointOnObject(g50,g47)
    c: Coincident(g51,g46)
    c: PointOnObject(g51,g46)
    c: Coincident(g52,g33)
    c: PointOnObject(g52,g37)
    c: Coincident(g53,g45)
    c: PointOnObject(g53,g45)
    c: Coincident(g54,g44)
    c: PointOnObject(g54,g44)
    c: Coincident(g55,g34)
    c: PointOnObject(g55,g38)
    c: Coincident(g56,g43)
    c: PointOnObject(g56,g43)
    c: Coincident(g57,g42)
    c: PointOnObject(g57,g42)
    c: Coincident(g58,g32)
    c: PointOnObject(g58,g39)
    c: Coincident(g59,g41)
    c: PointOnObject(g59,g41)
    c: Coincident(g49,g48)
    c: Coincident(g48,g50)
    c: Coincident(g51,g52)
    c: Coincident(g52,g53)
    c: Coincident(g54,g55)
    c: Coincident(g55,g56)
    c: Coincident(g57,g58)
    c: Coincident(g58,g59)
    c: PointOnObject(g60,g32)
    c: Horizontal(g60)
    c: PointOnObject(g61,g33)
    c: Vertical(g61)
    c: PointOnObject(g62,g34)
    c: Horizontal(g62)
    c: PointOnObject(g63,g35)
    c: Vertical(g63)
    c: Coincident(g59,g60)
    c: Coincident(g60,g49)
    c: Coincident(g50,g61)
    c: Coincident(g61,g51)
    c: Coincident(g53,g62)
    c: Coincident(g54,g62)
    c: Coincident(g56,g63)
    c: Coincident(g57,g63)
FEATURE [PartDesign::Pocket] Pocket
  BaseFeature = -> Pad
  Length = 10
  Length2 = 100
  Profile = -> Sketch002
  Type = 0
FEATURE [Sketcher::SketchObject] Sketch003
  MapMode = 5
  Placement = pos=(0,0,2) rot=(0,0,1;0rad)
  Support = -> [Pocket]
  expr: Constraints[133] = Sketch002.Constraints[133]
  expr: Constraints[130] = Sketch002.Constraints[130]
  expr: Constraints[112] = Sketch002.Constraints[112]
  expr: Constraints[127] = Sketch002.Constraints[127]
  expr: Constraints[124] = Sketch002.Constraints[124]
  expr: Constraints[110] = Sketch002.Constraints[110]
  expr: Constraints[51] = Sketch002.Constraints[51]
  expr: Constraints[100] = Sketch002.Constraints[100]
  expr: Constraints[77] = Sketch002.Constraints[77]
  expr: Constraints[89] = Sketch002.Constraints[89]
  expr: Constraints[85] = Sketch002.Constraints[85]
  expr: Constraints[118] = Sketch002.Constraints[118]
  expr: Constraints[111] = Sketch002.Constraints[111]
  expr: Constraints[103] = Sketch002.Constraints[103]
  expr: Constraints[71] = Sketch002.Constraints[71]
  expr: Constraints[102] = Sketch002.Constraints[102]
  expr: Constraints[49] = Sketch002.Constraints[49]
  expr: Constraints[69] = Sketch002.Constraints[69]
  expr: Constraints[75] = Sketch002.Constraints[75]
  expr: Constraints[73] = Sketch002.Constraints[73]
  expr: Constraints[47] = Sketch002.Constraints[47]
  expr: Constraints[31] = Sketch002.Constraints[31]
  expr: Constraints[40] = Sketch002.Constraints[40]
  expr: Constraints[116] = Sketch002.Constraints[116]
  expr: Constraints[30] = Sketch002.Constraints[30]
  expr: Constraints[29] = Sketch002.Constraints[29]
  expr: Constraints[121] = Sketch002.Constraints[121]
  expr: Constraints[28] = Sketch002.Constraints[28]
  expr: Constraints[21] = Sketch002.Constraints[21]
  expr: Constraints[20] = Sketch002.Constraints[20]
  expr: Constraints[42] = Sketch002.Constraints[42]
  expr: Constraints[43] = Sketch002.Constraints[43]
  expr: Constraints[101] = Sketch002.Constraints[101]
  expr: Constraints[108] = Sketch002.Constraints[108]
  expr: Constraints[45] = Sketch002.Constraints[45]
  expr: Constraints[41] = Sketch002.Constraints[41]
  expr: Constraints[9] = Sketch002.Constraints[9]
  expr: Constraints[81] = Sketch002.Constraints[81]
  expr: Constraints[109] = Sketch002.Constraints[109]
  expr: Constraints[8] = Sketch002.Constraints[8]
  sketch-geometry (92):
    g0: LineSegment [constr] StartX=-32.5 StartY=15 StartZ=0 EndX=32.5 EndY=15 EndZ=0
    g1: LineSegment [constr] StartX=32.5 StartY=15 StartZ=0 EndX=32.5 EndY=-15 EndZ=0
    g2: LineSegment [constr] StartX=32.5 StartY=-15 StartZ=0 EndX=-32.5 EndY=-15 EndZ=0
    g3: LineSegment [constr] StartX=-32.5 StartY=-15 StartZ=0 EndX=-32.5 EndY=15 EndZ=0
    g4: LineSegment [constr] StartX=-29 StartY=11.5 StartZ=0 EndX=29 EndY=11.5 EndZ=0
    g5: LineSegment [constr] StartX=29 StartY=11.5 StartZ=0 EndX=29 EndY=-11.5 EndZ=0
    g6: LineSegment [constr] StartX=29 StartY=-11.5 StartZ=0 EndX=-29 EndY=-11.5 EndZ=0
    g7: LineSegment [constr] StartX=-29 StartY=-11.5 StartZ=0 EndX=-29 EndY=11.5 EndZ=0
    g8: Circle [constr] CenterX=-29 CenterY=11.5 CenterZ=0 NormalX=0 NormalY=0 NormalZ=1 AngleXU=0 Radius=1.375
    g9: Circle [constr] CenterX=29 CenterY=11.5 CenterZ=0 NormalX=0 NormalY=0 NormalZ=1 AngleXU=0 Radius=1.375
    g10: Circle [constr] CenterX=29 CenterY=-11.5 CenterZ=0 NormalX=0 NormalY=0 NormalZ=1 AngleXU=0 Radius=1.375
    g11: Circle [constr] CenterX=-29 CenterY=-11.5 CenterZ=0 NormalX=0 NormalY=0 NormalZ=1 AngleXU=0 Radius=1.375
    g12: LineSegment [constr] StartX=-29.5 StartY=12 StartZ=0 EndX=29.5 EndY=12 EndZ=0
    g13: LineSegment [constr] StartX=29.5 StartY=12 StartZ=0 EndX=29.5 EndY=-12 EndZ=0
    g14: LineSegment [constr] StartX=29.5 StartY=-12 StartZ=0 EndX=-29.5 EndY=-12 EndZ=0
    g15: LineSegment [constr] StartX=-29.5 StartY=-12 StartZ=0 EndX=-29.5 EndY=12 EndZ=0
    g16: ArcOfCircle [constr] CenterX=-29.5 CenterY=12 CenterZ=0 NormalX=0 NormalY=0 NormalZ=1 AngleXU=0 Radius=3 StartAngle=1.5708 EndAngle=3.14159
    g17: ArcOfCircle [constr] CenterX=29.5 CenterY=12 CenterZ=0 NormalX=0 NormalY=0 NormalZ=1 AngleXU=0 Radius=3 StartAngle=3.6972e-08 EndAngle=1.5708
    g18: ArcOfCircle [constr] CenterX=29.5 CenterY=-12 CenterZ=0 NormalX=0 NormalY=0 NormalZ=1 AngleXU=0 Radius=3 StartAngle=4.71239 EndAngle=6.28319
    g19: ArcOfCircle [constr] CenterX=-29.5 CenterY=-12 CenterZ=0 NormalX=0 NormalY=0 NormalZ=1 AngleXU=0 Radius=3 StartAngle=3.14159 EndAngle=4.71239
    g20: LineSegment [constr] StartX=-29.5 StartY=15 StartZ=0 EndX=29.5 EndY=15 EndZ=0
    g21: LineSegment [constr] StartX=32.5 StartY=12 StartZ=0 EndX=32.5 EndY=-12 EndZ=0
    g22: LineSegment [constr] StartX=29.5 StartY=-15 StartZ=0 EndX=-29.5 EndY=-15 EndZ=0
    g23: LineSegment [constr] StartX=-32.5 StartY=-12 StartZ=0 EndX=-32.5 EndY=12 EndZ=0
    g24: ArcOfCircle [constr] CenterX=-29.5 CenterY=12 CenterZ=0 NormalX=0 NormalY=0 NormalZ=1 AngleXU=0 Radius=3.3 StartAngle=1.5708 EndAngle=3.14159
    g25: ArcOfCircle [constr] CenterX=29.5 CenterY=12 CenterZ=0 NormalX=0 NormalY=0 NormalZ=1 AngleXU=0 Radius=3.3 StartAngle=-4.27e-10 EndAngle=1.5708
    g26: ArcOfCircle [constr] CenterX=29.5 CenterY=-12 CenterZ=0 NormalX=0 NormalY=0 NormalZ=1 AngleXU=0 Radius=3.3 StartAngle=4.71239 EndAngle=6.28319
    g27: ArcOfCircle [constr] CenterX=-29.5 CenterY=-12 CenterZ=0 NormalX=0 NormalY=0 NormalZ=1 AngleXU=0 Radius=3.3 StartAngle=3.14159 EndAngle=4.71239
    g28: LineSegment [constr] StartX=-32.8 StartY=12 StartZ=0 EndX=-32.8 EndY=-12 EndZ=0
    g29: LineSegment [constr] StartX=-29.5 StartY=15.3 StartZ=0 EndX=29.5 EndY=15.3 EndZ=0
    g30: LineSegment [constr] StartX=32.8 StartY=12 StartZ=0 EndX=32.8 EndY=-12 EndZ=0
    g31: LineSegment [constr] StartX=29.5 StartY=-15.3 StartZ=0 EndX=-29.5 EndY=-15.3 EndZ=0
    g32: LineSegment [constr] StartX=-34.8 StartY=17.3 StartZ=0 EndX=34.8 EndY=17.3 EndZ=0
    g33: LineSegment [constr] StartX=34.8 StartY=17.3 StartZ=0 EndX=34.8 EndY=-17.3 EndZ=0
    g34: LineSegment [constr] StartX=34.8 StartY=-17.3 StartZ=0 EndX=-34.8 EndY=-17.3 EndZ=0
    g35: LineSegment [constr] StartX=-34.8 StartY=-17.3 StartZ=0 EndX=-34.8 EndY=17.3 EndZ=0
    g36: Circle [constr] CenterX=34.8 CenterY=17.3 CenterZ=0 NormalX=0 NormalY=0 NormalZ=1 AngleXU=0 Radius=5
    g37: Circle [constr] CenterX=34.8 CenterY=-17.3 CenterZ=0 NormalX=0 NormalY=0 NormalZ=1 AngleXU=0 Radius=5
    g38: Circle [constr] CenterX=-34.8 CenterY=-17.3 CenterZ=0 NormalX=0 NormalY=0 NormalZ=1 AngleXU=0 Radius=5
    g39: Circle [constr] CenterX=-34.8 CenterY=17.3 CenterZ=0 NormalX=0 NormalY=0 NormalZ=1 AngleXU=0 Radius=5
    g40: Circle [constr] CenterX=27.3838 CenterY=20.3 CenterZ=0 NormalX=0 NormalY=0 NormalZ=1 AngleXU=0 Radius=3
    g41: Circle [constr] CenterX=-27.3838 CenterY=20.3 CenterZ=0 NormalX=0 NormalY=0 NormalZ=1 AngleXU=0 Radius=3
    g42: Circle [constr] CenterX=-37.8 CenterY=9.8838 CenterZ=0 NormalX=0 NormalY=0 NormalZ=1 AngleXU=0 Radius=3
    g43: Circle [constr] CenterX=-37.8 CenterY=-9.8838 CenterZ=0 NormalX=0 NormalY=0 NormalZ=1 AngleXU=0 Radius=3
    g44: Circle [constr] CenterX=-27.3838 CenterY=-20.3 CenterZ=0 NormalX=0 NormalY=0 NormalZ=1 AngleXU=0 Radius=3
    g45: Circle [constr] CenterX=27.3838 CenterY=-20.3 CenterZ=0 NormalX=0 NormalY=0 NormalZ=1 AngleXU=0 Radius=3
    g46: Circle [constr] CenterX=37.8 CenterY=-9.8838 CenterZ=0 NormalX=0 NormalY=0 NormalZ=1 AngleXU=0 Radius=3
    g47: Circle [constr] CenterX=37.8 CenterY=9.8838 CenterZ=0 NormalX=0 NormalY=0 NormalZ=1 AngleXU=0 Radius=3
    g48: ArcOfCircle [constr] CenterX=34.8 CenterY=17.3 CenterZ=0 NormalX=0 NormalY=0 NormalZ=1 AngleXU=0 Radius=5 StartAngle=5.09679 EndAngle=9.04038
    g49: ArcOfCircle [constr] CenterX=27.3838 CenterY=20.3 CenterZ=0 NormalX=0 NormalY=0 NormalZ=1 AngleXU=0 Radius=3 StartAngle=4.71239 EndAngle=5.89879
    g50: ArcOfCircle [constr] CenterX=37.8 CenterY=9.8838 CenterZ=0 NormalX=0 NormalY=0 NormalZ=1 AngleXU=0 Radius=3 StartAngle=1.95519 EndAngle=3.14159
    g51: ArcOfCircle [constr] CenterX=37.8 CenterY=-9.8838 CenterZ=0 NormalX=0 NormalY=0 NormalZ=1 AngleXU=0 Radius=3 StartAngle=3.14159 EndAngle=4.32799
    g52: ArcOfCircle [constr] CenterX=34.8 CenterY=-17.3 CenterZ=0 NormalX=0 NormalY=0 NormalZ=1 AngleXU=0 Radius=5 StartAngle=3.52599 EndAngle=7.46958
    g53: ArcOfCircle [constr] CenterX=27.3838 CenterY=-20.3 CenterZ=0 NormalX=0 NormalY=0 NormalZ=1 AngleXU=0 Radius=3 StartAngle=0.384397 EndAngle=1.5708
    g54: ArcOfCircle [constr] CenterX=-27.3838 CenterY=-20.3 CenterZ=0 NormalX=0 NormalY=0 NormalZ=1 AngleXU=0 Radius=3 StartAngle=1.5708 EndAngle=2.7572
    g55: ArcOfCircle [constr] CenterX=-34.8 CenterY=-17.3 CenterZ=0 NormalX=0 NormalY=0 NormalZ=1 AngleXU=0 Radius=5 StartAngle=1.95519 EndAngle=5.89879
    g56: ArcOfCircle [constr] CenterX=-37.8 CenterY=-9.8838 CenterZ=0 NormalX=0 NormalY=0 NormalZ=1 AngleXU=0 Radius=3 StartAngle=5.09678 EndAngle=6.28319
    g57: ArcOfCircle [constr] CenterX=-37.8 CenterY=9.8838 CenterZ=0 NormalX=0 NormalY=0 NormalZ=1 AngleXU=0 Radius=3 StartAngle=4.4909e-08 EndAngle=1.1864
    g58: ArcOfCircle [constr] CenterX=-34.8 CenterY=17.3 CenterZ=0 NormalX=0 NormalY=0 NormalZ=1 AngleXU=0 Radius=5 StartAngle=0.384397 EndAngle=4.32799
    g59: ArcOfCircle [constr] CenterX=-27.3838 CenterY=20.3 CenterZ=0 NormalX=0 NormalY=0 NormalZ=1 AngleXU=0 Radius=3 StartAngle=3.52599 EndAngle=4.71239
    g60: LineSegment [constr] StartX=-27.3838 StartY=17.3 StartZ=0 EndX=27.3838 EndY=17.3 EndZ=0
    g61: LineSegment [constr] StartX=34.8 StartY=9.8838 StartZ=0 EndX=34.8 EndY=-9.8838 EndZ=0
    g62: LineSegment [constr] StartX=27.3838 StartY=-17.3 StartZ=0 EndX=-27.3838 EndY=-17.3 EndZ=0
    g63: LineSegment [constr] StartX=-34.8 StartY=-9.8838 StartZ=0 EndX=-34.8 EndY=9.8838 EndZ=0
    g64: ArcOfCircle CenterX=29 CenterY=11.5 CenterZ=0 NormalX=0 NormalY=0 NormalZ=1 AngleXU=0 Radius=3 StartAngle=3.14352 EndAngle=4.71046
    g65: ArcOfCircle CenterX=29.5 CenterY=12 CenterZ=0 NormalX=0 NormalY=0 NormalZ=1 AngleXU=0 Radius=3.3 StartAngle=2.17631e-07 EndAngle=1.5708
    g66: LineSegment StartX=26 StartY=15.3 StartZ=0 EndX=29.5 EndY=15.3 EndZ=0
    g67: LineSegment StartX=32.8 StartY=12 StartZ=0 EndX=32.8 EndY=8.50001 EndZ=0
    g68: LineSegment StartX=26 StartY=15.3 StartZ=0 EndX=26 EndY=11.4942 EndZ=0
    g69: LineSegment StartX=28.9942 StartY=8.50001 StartZ=0 EndX=32.8 EndY=8.50001 EndZ=0
    g70: LineSegment [constr] StartX=-43.6068 StartY=0 StartZ=0 EndX=51.9839 EndY=0 EndZ=0
    g71: LineSegment [constr] StartX=0 StartY=-19.8111 StartZ=0 EndX=0 EndY=22.459 EndZ=0
    g72: LineSegment StartX=26 StartY=-15.3 StartZ=0 EndX=26 EndY=-11.4942 EndZ=0
    g73: ArcOfCircle CenterX=29 CenterY=-11.5 CenterZ=0 NormalX=0 NormalY=0 NormalZ=1 AngleXU=0 Radius=3 StartAngle=1.57273 EndAngle=3.13966
    g74: LineSegment StartX=28.9942 StartY=-8.50001 StartZ=0 EndX=32.8 EndY=-8.50001 EndZ=0
    g75: LineSegment StartX=26 StartY=-15.3 StartZ=0 EndX=29.5 EndY=-15.3 EndZ=0
    g76: ArcOfCircle CenterX=29.5 CenterY=-12 CenterZ=0 NormalX=0 NormalY=0 NormalZ=1 AngleXU=0 Radius=3.3 StartAngle=4.71238 EndAngle=6.28319
    g77: LineSegment StartX=32.8 StartY=-12 StartZ=0 EndX=32.8 EndY=-8.50001 EndZ=0
    g78: LineSegment StartX=-28.9942 StartY=-8.50001 StartZ=0 EndX=-32.8 EndY=-8.50001 EndZ=0
    g79: LineSegment StartX=-32.8 StartY=-12 StartZ=0 EndX=-32.8 EndY=-8.50001 EndZ=0
    g80: ArcOfCircle CenterX=-29.5 CenterY=-12 CenterZ=0 NormalX=0 NormalY=0 NormalZ=1 AngleXU=0 Radius=3.3 StartAngle=3.14159 EndAngle=4.71239
    g81: LineSegment StartX=-26 StartY=-15.3 StartZ=0 EndX=-29.5 EndY=-15.3 EndZ=0
    g82: LineSegment StartX=-26 StartY=-15.3 StartZ=0 EndX=-26 EndY=-11.4942 EndZ=0
    g83: ArcOfCircle CenterX=-29 CenterY=-11.5 CenterZ=0 NormalX=0 NormalY=0 NormalZ=1 AngleXU=0 Radius=3 StartAngle=0.00192871 EndAngle=1.56886
    g84: LineSegment StartX=-28.9942 StartY=8.50001 StartZ=0 EndX=-32.8 EndY=8.50001 EndZ=0
    g85: LineSegment StartX=-32.8 StartY=12 StartZ=0 EndX=-32.8 EndY=8.50001 EndZ=0
    g86: ArcOfCircle CenterX=-29.5 CenterY=12 CenterZ=0 NormalX=0 NormalY=0 NormalZ=1 AngleXU=0 Radius=3.3 StartAngle=1.57079 EndAngle=3.14159
    g87: LineSegment StartX=-26 StartY=15.3 StartZ=0 EndX=-29.5 EndY=15.3 EndZ=0
    g88: LineSegment StartX=-26 StartY=15.3 StartZ=0 EndX=-26 EndY=11.4942 EndZ=0
    g89: ArcOfCircle CenterX=-29 CenterY=11.5 CenterZ=0 NormalX=0 NormalY=0 NormalZ=1 AngleXU=0 Radius=3 StartAngle=4.71432 EndAngle=6.28126
    g90: Circle CenterX=29 CenterY=11.5 CenterZ=0 NormalX=0 NormalY=0 NormalZ=1 AngleXU=0 Radius=0.5
    g91: Circle CenterX=-29 CenterY=-11.5 CenterZ=0 NormalX=0 NormalY=0 NormalZ=1 AngleXU=0 Radius=0.5
  constraints (241):
    c: Coincident(g0,g1)
    c: Coincident(g1,g2)
    c: Coincident(g2,g3)
    c: Coincident(g3,g0)
    c: Horizontal(g0)
    c: Horizontal(g2)
    c: Vertical(g1)
    c: Vertical(g3)
    c: DistanceX(g0,g0) = 65
    c: DistanceY(g1,g1) = 30
    c: Symmetric(g0,g0,g-2)
    c: Symmetric(g0,g1,g-1)
    c: Coincident(g4,g5)
    c: Coincident(g5,g6)
    c: Coincident(g6,g7)
    c: Coincident(g7,g4)
    c: Horizontal(g4)
    c: Horizontal(g6)
    c: Vertical(g5)
    c: Vertical(g7)
    c: DistanceX(g4,g4) = 58
    c: DistanceY(g5,g5) = 23
    c: Symmetric(g4,g5,g-1)
    c: Symmetric(g4,g4,g-2)
    c: Coincident(g8,g4)
    c: Coincident(g9,g4)
    c: Coincident(g10,g5)
    c: Coincident(g11,g6)
    c: Radius(g11) = 1.375
    c: Radius(g8) = 1.375
    c: Radius(g9) = 1.375
    c: Radius(g10) = 1.375
    c: Coincident(g12,g13)
    c: Coincident(g13,g14)
    c: Coincident(g14,g15)
    c: Coincident(g15,g12)
    c: Horizontal(g12)
    c: Horizontal(g14)
    c: Vertical(g13)
    c: Vertical(g15)
    c: DistanceX(g4,g12) = 0.5
    c: DistanceY(g4,g12) = 0.5
    c: DistanceY(g13,g5) = 0.5
    c: DistanceX(g14,g6) = 0.5
    c: Coincident(g16,g12)
    c: Radius(g16) = 3
    c: Coincident(g17,g12)
    c: Radius(g17) = 3
    c: Coincident(g18,g13)
    c: Radius(g18) = 3
    c: Coincident(g19,g14)
    c: Radius(g19) = 3
    c: PointOnObject(g16,g0)
    c: PointOnObject(g17,g1)
    c: PointOnObject(g18,g2)
    c: PointOnObject(g19,g3)
    c: Coincident(g20,g16)
    c: Horizontal(g20)
    c: Coincident(g20,g17)
    c: Coincident(g21,g17)
    c: Vertical(g21)
    c: Coincident(g18,g21)
    c: Coincident(g22,g18)
    c: Horizontal(g22)
    c: Coincident(g19,g22)
    c: Coincident(g23,g19)
    c: Vertical(g23)
    c: Coincident(g23,g16)
    c: Coincident(g24,g12)
    c: Radius(g24) = 3.3
    c: Coincident(g25,g12)
    c: Radius(g25) = 3.3
    c: Coincident(g26,g13)
    c: Radius(g26) = 3.3
    c: Coincident(g27,g14)
    c: Radius(g27) = 3.3
    c: Vertical(g28)
    c: DistanceX(g28,g2) = 0.3
    c: Coincident(g27,g28)
    c: Coincident(g28,g24)
    c: Horizontal(g29)
    c: DistanceY(g0,g29) = 0.3
    c: Coincident(g24,g29)
    c: Coincident(g25,g29)
    c: Vertical(g30)
    c: DistanceX(g0,g30) = 0.3
    c: Coincident(g25,g30)
    c: Coincident(g30,g26)
    c: Horizontal(g31)
    c: DistanceY(g31,g1) = 0.3
    c: Coincident(g31,g26)
    c: Coincident(g31,g27)
    c: Coincident(g32,g33)
    c: Coincident(g33,g34)
    c: Coincident(g34,g35)
    c: Coincident(g35,g32)
    c: Horizontal(g32)
    c: Horizontal(g34)
    c: Vertical(g33)
    c: Vertical(g35)
    c: DistanceY(g25,g32) = 2
    c: DistanceX(g25,g32) = 2
    c: DistanceY(g33,g26) = 2
    c: DistanceX(g34,g27) = 2
    c: Coincident(g36,g32)
    c: Coincident(g37,g33)
    c: Coincident(g38,g34)
    c: Coincident(g39,g32)
    c: Radius(g39) = 5
    c: Radius(g38) = 5
    c: Radius(g37) = 5
    c: Radius(g36) = 5
    c: Radius(g40) = 3
    c: Tangent(g40,g36)
    c: Tangent(g40,g32)
    c: Tangent(g47,g36)
    c: Radius(g47) = 3
    c: Tangent(g47,g33)
    c: Radius(g46) = 3
    c: Tangent(g46,g37)
    c: Tangent(g46,g33)
    c: Radius(g45) = 3
    c: Tangent(g45,g37)
    c: Tangent(g45,g34)
    c: Radius(g44) = 3
    c: Tangent(g44,g34)
    c: Tangent(g44,g38)
    c: Radius(g43) = 3
    c: Tangent(g43,g38)
    c: Tangent(g43,g35)
    c: Radius(g42) = 3
    c: Tangent(g42,g35)
    c: Tangent(g42,g39)
    c: Radius(g41) = 3
    c: Tangent(g41,g32)
    c: Tangent(g41,g39)
    c: Coincident(g48,g32)
    c: PointOnObject(g48,g36)
    c: Coincident(g49,g40)
    c: PointOnObject(g49,g40)
    c: Coincident(g50,g47)
    c: PointOnObject(g50,g47)
    c: Coincident(g51,g46)
    c: PointOnObject(g51,g46)
    c: Coincident(g52,g33)
    c: PointOnObject(g52,g37)
    c: Coincident(g53,g45)
    c: PointOnObject(g53,g45)
    c: Coincident(g54,g44)
    c: PointOnObject(g54,g44)
    c: Coincident(g55,g34)
    c: PointOnObject(g55,g38)
    c: Coincident(g56,g43)
    c: PointOnObject(g56,g43)
    c: Coincident(g57,g42)
    c: PointOnObject(g57,g42)
    c: Coincident(g58,g32)
    c: PointOnObject(g58,g39)
    c: Coincident(g59,g41)
    c: PointOnObject(g59,g41)
    c: Coincident(g49,g48)
    c: Coincident(g48,g50)
    c: Coincident(g51,g52)
    c: Coincident(g52,g53)
    c: Coincident(g54,g55)
    c: Coincident(g55,g56)
    c: Coincident(g57,g58)
    c: Coincident(g58,g59)
    c: PointOnObject(g60,g32)
    c: Horizontal(g60)
    c: PointOnObject(g61,g33)
    c: Vertical(g61)
    c: PointOnObject(g62,g34)
    c: Horizontal(g62)
    c: PointOnObject(g63,g35)
    c: Vertical(g63)
    c: Coincident(g59,g60)
    c: Coincident(g60,g49)
    c: Coincident(g50,g61)
    c: Coincident(g61,g51)
    c: Coincident(g53,g62)
    c: Coincident(g54,g62)
    c: Coincident(g56,g63)
    c: Coincident(g57,g63)
    c: Coincident(g64,g4)
    c: Radius(g64) = 3
    c: Coincident(g65,g12)
    c: PointOnObject(g66,g29)
    c: Horizontal(g66)
    c: Coincident(g65,g66)
    c: PointOnObject(g65,g25)
    c: PointOnObject(g67,g30)
    c: Vertical(g67)
    c: Coincident(g67,g65)
    c: Vertical(g68)
    c: Coincident(g68,g64)
    c: Coincident(g68,g66)
    c: Horizontal(g69)
    c: Coincident(g64,g69)
    c: Coincident(g67,g69)
    c: PointOnObject(g70,g-1)
    c: Horizontal(g70)
    c: PointOnObject(g71,g-2)
    c: Vertical(g71)
    c: Radius(g73) = 3
    c: Horizontal(g75)
    c: Coincident(g76,g75)
    c: Vertical(g77)
    c: Coincident(g77,g76)
    c: Vertical(g72)
    c: Coincident(g72,g73)
    c: Coincident(g72,g75)
    c: Horizontal(g74)
    c: Coincident(g73,g74)
    c: Coincident(g77,g74)
    c: Radius(g89) = 3
    c: Horizontal(g87)
    c: Coincident(g86,g87)
    c: Vertical(g85)
    c: Coincident(g85,g86)
    c: Vertical(g88)
    c: Coincident(g88,g89)
    c: Coincident(g88,g87)
    c: Horizontal(g84)
    c: Coincident(g89,g84)
    c: Coincident(g85,g84)
    c: Radius(g83) = 3
    c: Horizontal(g81)
    c: Coincident(g80,g81)
    c: Vertical(g79)
    c: Coincident(g79,g80)
    c: Vertical(g82)
    c: Coincident(g82,g83)
    c: Coincident(g82,g81)
    c: Horizontal(g78)
    c: Coincident(g83,g78)
    c: Coincident(g79,g78)
    c: Coincident(g90,g4)
    c: Radius(g90) = 0.5
    c: Coincident(g91,g6)
    c: Radius(g91) = 0.5
FEATURE [PartDesign::Pad] Pad001
  BaseFeature = -> Pocket
  Length = 5.5
  Length2 = 100
  Profile = -> Sketch003
  Type = 0
FEATURE [Sketcher::SketchObject] Sketch004
  MapMode = 5
  Placement = pos=(0,0,12) rot=(0,0,1;0rad)
  Support = -> [Pad001]
  expr: Constraints[133] = Sketch001.Constraints[133]
  expr: Constraints[130] = Sketch001.Constraints[130]
  expr: Constraints[112] = Sketch001.Constraints[112]
  expr: Constraints[127] = Sketch001.Constraints[127]
  expr: Constraints[124] = Sketch001.Constraints[124]
  expr: Constraints[110] = Sketch001.Constraints[110]
  expr: Constraints[51] = Sketch001.Constraints[51]
  expr: Constraints[100] = Sketch001.Constraints[100]
  expr: Constraints[77] = Sketch001.Constraints[77]
  expr: Constraints[89] = Sketch001.Constraints[89]
  expr: Constraints[118] = Sketch001.Constraints[118]
  expr: Constraints[85] = Sketch001.Constraints[85]
  expr: Constraints[103] = Sketch001.Constraints[103]
  expr: Constraints[111] = Sketch001.Constraints[111]
  expr: Constraints[71] = Sketch001.Constraints[71]
  expr: Constraints[49] = Sketch001.Constraints[49]
  expr: Constraints[102] = Sketch001.Constraints[102]
  expr: Constraints[69] = Sketch001.Constraints[69]
  expr: Constraints[47] = Sketch001.Constraints[47]
  expr: Constraints[73] = Sketch001.Constraints[73]
  expr: Constraints[75] = Sketch001.Constraints[75]
  expr: Constraints[31] = Sketch001.Constraints[31]
  expr: Constraints[116] = Sketch001.Constraints[116]
  expr: Constraints[40] = Sketch001.Constraints[40]
  expr: Constraints[30] = Sketch001.Constraints[30]
  expr: Constraints[29] = Sketch001.Constraints[29]
  expr: Constraints[121] = Sketch001.Constraints[121]
  expr: Constraints[28] = Sketch001.Constraints[28]
  expr: Constraints[21] = Sketch001.Constraints[21]
  expr: Constraints[20] = Sketch001.Constraints[20]
  expr: Constraints[108] = Sketch001.Constraints[108]
  expr: Constraints[45] = Sketch001.Constraints[45]
  expr: Constraints[42] = Sketch001.Constraints[42]
  expr: Constraints[43] = Sketch001.Constraints[43]
  expr: Constraints[101] = Sketch001.Constraints[101]
  expr: Constraints[109] = Sketch001.Constraints[109]
  expr: Constraints[41] = Sketch001.Constraints[41]
  expr: Constraints[9] = Sketch001.Constraints[9]
  expr: Constraints[81] = Sketch001.Constraints[81]
  expr: Constraints[8] = Sketch001.Constraints[8]
  sketch-geometry (68):
    g0: LineSegment [constr] StartX=-32.5 StartY=15 StartZ=0 EndX=32.5 EndY=15 EndZ=0
    g1: LineSegment [constr] StartX=32.5 StartY=15 StartZ=0 EndX=32.5 EndY=-15 EndZ=0
    g2: LineSegment [constr] StartX=32.5 StartY=-15 StartZ=0 EndX=-32.5 EndY=-15 EndZ=0
    g3: LineSegment [constr] StartX=-32.5 StartY=-15 StartZ=0 EndX=-32.5 EndY=15 EndZ=0
    g4: LineSegment [constr] StartX=-29 StartY=11.5 StartZ=0 EndX=29 EndY=11.5 EndZ=0
    g5: LineSegment [constr] StartX=29 StartY=11.5 StartZ=0 EndX=29 EndY=-11.5 EndZ=0
    g6: LineSegment [constr] StartX=29 StartY=-11.5 StartZ=0 EndX=-29 EndY=-11.5 EndZ=0
    g7: LineSegment [constr] StartX=-29 StartY=-11.5 StartZ=0 EndX=-29 EndY=11.5 EndZ=0
    g8: Circle [constr] CenterX=-29 CenterY=11.5 CenterZ=0 NormalX=0 NormalY=0 NormalZ=1 AngleXU=0 Radius=1.375
    g9: Circle [constr] CenterX=29 CenterY=11.5 CenterZ=0 NormalX=0 NormalY=0 NormalZ=1 AngleXU=0 Radius=1.375
    g10: Circle [constr] CenterX=29 CenterY=-11.5 CenterZ=0 NormalX=0 NormalY=0 NormalZ=1 AngleXU=0 Radius=1.375
    g11: Circle [constr] CenterX=-29 CenterY=-11.5 CenterZ=0 NormalX=0 NormalY=0 NormalZ=1 AngleXU=0 Radius=1.375
    g12: LineSegment [constr] StartX=-29.5 StartY=12 StartZ=0 EndX=29.5 EndY=12 EndZ=0
    g13: LineSegment [constr] StartX=29.5 StartY=12 StartZ=0 EndX=29.5 EndY=-12 EndZ=0
    g14: LineSegment [constr] StartX=29.5 StartY=-12 StartZ=0 EndX=-29.5 EndY=-12 EndZ=0
    g15: LineSegment [constr] StartX=-29.5 StartY=-12 StartZ=0 EndX=-29.5 EndY=12 EndZ=0
    g16: ArcOfCircle [constr] CenterX=-29.5 CenterY=12 CenterZ=0 NormalX=0 NormalY=0 NormalZ=1 AngleXU=0 Radius=3 StartAngle=1.5708 EndAngle=3.14159
    g17: ArcOfCircle [constr] CenterX=29.5 CenterY=12 CenterZ=0 NormalX=0 NormalY=0 NormalZ=1 AngleXU=0 Radius=3 StartAngle=2.8425e-08 EndAngle=1.5708
    g18: ArcOfCircle [constr] CenterX=29.5 CenterY=-12 CenterZ=0 NormalX=0 NormalY=0 NormalZ=1 AngleXU=0 Radius=3 StartAngle=4.71239 EndAngle=6.28319
    g19: ArcOfCircle [constr] CenterX=-29.5 CenterY=-12 CenterZ=0 NormalX=0 NormalY=0 NormalZ=1 AngleXU=0 Radius=3 StartAngle=3.14159 EndAngle=4.71239
    g20: LineSegment [constr] StartX=-29.5 StartY=15 StartZ=0 EndX=29.5 EndY=15 EndZ=0
    g21: LineSegment [constr] StartX=32.5 StartY=12 StartZ=0 EndX=32.5 EndY=-12 EndZ=0
    g22: LineSegment [constr] StartX=29.5 StartY=-15 StartZ=0 EndX=-29.5 EndY=-15 EndZ=0
    g23: LineSegment [constr] StartX=-32.5 StartY=-12 StartZ=0 EndX=-32.5 EndY=12 EndZ=0
    g24: ArcOfCircle [constr] CenterX=-29.5 CenterY=12 CenterZ=0 NormalX=0 NormalY=0 NormalZ=1 AngleXU=0 Radius=3.3 StartAngle=1.5708 EndAngle=3.14159
    g25: ArcOfCircle [constr] CenterX=29.5 CenterY=12 CenterZ=0 NormalX=0 NormalY=0 NormalZ=1 AngleXU=0 Radius=3.3 StartAngle=-2.2e-10 EndAngle=1.5708
    g26: ArcOfCircle [constr] CenterX=29.5 CenterY=-12 CenterZ=0 NormalX=0 NormalY=0 NormalZ=1 AngleXU=0 Radius=3.3 StartAngle=4.71239 EndAngle=6.28319
    g27: ArcOfCircle [constr] CenterX=-29.5 CenterY=-12 CenterZ=0 NormalX=0 NormalY=0 NormalZ=1 AngleXU=0 Radius=3.3 StartAngle=3.14159 EndAngle=4.71239
    g28: LineSegment [constr] StartX=-32.8 StartY=12 StartZ=0 EndX=-32.8 EndY=-12 EndZ=0
    g29: LineSegment [constr] StartX=-29.5 StartY=15.3 StartZ=0 EndX=29.5 EndY=15.3 EndZ=0
    g30: LineSegment [constr] StartX=32.8 StartY=12 StartZ=0 EndX=32.8 EndY=-12 EndZ=0
    g31: LineSegment [constr] StartX=29.5 StartY=-15.3 StartZ=0 EndX=-29.5 EndY=-15.3 EndZ=0
    g32: LineSegment [constr] StartX=-34.8 StartY=17.3 StartZ=0 EndX=34.8 EndY=17.3 EndZ=0
    g33: LineSegment [constr] StartX=34.8 StartY=17.3 StartZ=0 EndX=34.8 EndY=-17.3 EndZ=0
    g34: LineSegment [constr] StartX=34.8 StartY=-17.3 StartZ=0 EndX=-34.8 EndY=-17.3 EndZ=0
    g35: LineSegment [constr] StartX=-34.8 StartY=-17.3 StartZ=0 EndX=-34.8 EndY=17.3 EndZ=0
    g36: Circle [constr] CenterX=34.8 CenterY=17.3 CenterZ=0 NormalX=0 NormalY=0 NormalZ=1 AngleXU=0 Radius=5
    g37: Circle [constr] CenterX=34.8 CenterY=-17.3 CenterZ=0 NormalX=0 NormalY=0 NormalZ=1 AngleXU=0 Radius=5
    g38: Circle [constr] CenterX=-34.8 CenterY=-17.3 CenterZ=0 NormalX=0 NormalY=0 NormalZ=1 AngleXU=0 Radius=5
    g39: Circle [constr] CenterX=-34.8 CenterY=17.3 CenterZ=0 NormalX=0 NormalY=0 NormalZ=1 AngleXU=0 Radius=5
    g40: Circle [constr] CenterX=27.3838 CenterY=20.3 CenterZ=0 NormalX=0 NormalY=0 NormalZ=1 AngleXU=0 Radius=3
    g41: Circle [constr] CenterX=-27.3838 CenterY=20.3 CenterZ=0 NormalX=0 NormalY=0 NormalZ=1 AngleXU=0 Radius=3
    g42: Circle [constr] CenterX=-37.8 CenterY=9.8838 CenterZ=0 NormalX=0 NormalY=0 NormalZ=1 AngleXU=0 Radius=3
    g43: Circle [constr] CenterX=-37.8 CenterY=-9.8838 CenterZ=0 NormalX=0 NormalY=0 NormalZ=1 AngleXU=0 Radius=3
    g44: Circle [constr] CenterX=-27.3838 CenterY=-20.3 CenterZ=0 NormalX=0 NormalY=0 NormalZ=1 AngleXU=0 Radius=3
    g45: Circle [constr] CenterX=27.3838 CenterY=-20.3 CenterZ=0 NormalX=0 NormalY=0 NormalZ=1 AngleXU=0 Radius=3
    g46: Circle [constr] CenterX=37.8 CenterY=-9.8838 CenterZ=0 NormalX=0 NormalY=0 NormalZ=1 AngleXU=0 Radius=3
    g47: Circle [constr] CenterX=37.8 CenterY=9.8838 CenterZ=0 NormalX=0 NormalY=0 NormalZ=1 AngleXU=0 Radius=3
    g48: ArcOfCircle [constr] CenterX=34.8 CenterY=17.3 CenterZ=0 NormalX=0 NormalY=0 NormalZ=1 AngleXU=0 Radius=5 StartAngle=5.09679 EndAngle=9.04038
    g49: ArcOfCircle [constr] CenterX=27.3838 CenterY=20.3 CenterZ=0 NormalX=0 NormalY=0 NormalZ=1 AngleXU=0 Radius=3 StartAngle=4.71239 EndAngle=5.89879
    g50: ArcOfCircle [constr] CenterX=37.8 CenterY=9.8838 CenterZ=0 NormalX=0 NormalY=0 NormalZ=1 AngleXU=0 Radius=3 StartAngle=1.95519 EndAngle=3.14159
    g51: ArcOfCircle [constr] CenterX=37.8 CenterY=-9.8838 CenterZ=0 NormalX=0 NormalY=0 NormalZ=1 AngleXU=0 Radius=3 StartAngle=3.14159 EndAngle=4.32799
    g52: ArcOfCircle [constr] CenterX=34.8 CenterY=-17.3 CenterZ=0 NormalX=0 NormalY=0 NormalZ=1 AngleXU=0 Radius=5 StartAngle=3.52599 EndAngle=7.46958
    g53: ArcOfCircle [constr] CenterX=27.3838 CenterY=-20.3 CenterZ=0 NormalX=0 NormalY=0 NormalZ=1 AngleXU=0 Radius=3 StartAngle=0.384397 EndAngle=1.5708
    g54: ArcOfCircle [constr] CenterX=-27.3838 CenterY=-20.3 CenterZ=0 NormalX=0 NormalY=0 NormalZ=1 AngleXU=0 Radius=3 StartAngle=1.5708 EndAngle=2.7572
    g55: ArcOfCircle [constr] CenterX=-34.8 CenterY=-17.3 CenterZ=0 NormalX=0 NormalY=0 NormalZ=1 AngleXU=0 Radius=5 StartAngle=1.95519 EndAngle=5.89879
    g56: ArcOfCircle [constr] CenterX=-37.8 CenterY=-9.8838 CenterZ=0 NormalX=0 NormalY=0 NormalZ=1 AngleXU=0 Radius=3 StartAngle=5.09679 EndAngle=6.28319
    g57: ArcOfCircle [constr] CenterX=-37.8 CenterY=9.8838 CenterZ=0 NormalX=0 NormalY=0 NormalZ=1 AngleXU=0 Radius=3 StartAngle=6.28319 EndAngle=7.46958
    g58: ArcOfCircle [constr] CenterX=-34.8 CenterY=17.3 CenterZ=0 NormalX=0 NormalY=0 NormalZ=1 AngleXU=0 Radius=5 StartAngle=0.384397 EndAngle=4.32799
    g59: ArcOfCircle [constr] CenterX=-27.3838 CenterY=20.3 CenterZ=0 NormalX=0 NormalY=0 NormalZ=1 AngleXU=0 Radius=3 StartAngle=3.52599 EndAngle=4.71239
    g60: LineSegment [constr] StartX=-27.3838 StartY=17.3 StartZ=0 EndX=27.3838 EndY=17.3 EndZ=0
    g61: LineSegment [constr] StartX=34.8 StartY=9.8838 StartZ=0 EndX=34.8 EndY=-9.8838 EndZ=0
    g62: LineSegment [constr] StartX=27.3838 StartY=-17.3 StartZ=0 EndX=-27.3838 EndY=-17.3 EndZ=0
    g63: LineSegment [constr] StartX=-34.8 StartY=-9.8838 StartZ=0 EndX=-34.8 EndY=9.8838 EndZ=0
    g64: Circle CenterX=34.8 CenterY=17.3 CenterZ=0 NormalX=0 NormalY=0 NormalZ=1 AngleXU=0 Radius=3.2
    g65: Circle CenterX=34.8 CenterY=-17.3 CenterZ=0 NormalX=0 NormalY=0 NormalZ=1 AngleXU=0 Radius=3.2
    g66: Circle CenterX=-34.8 CenterY=-17.3 CenterZ=0 NormalX=0 NormalY=0 NormalZ=1 AngleXU=0 Radius=3.2
    g67: Circle CenterX=-34.8 CenterY=17.3 CenterZ=0 NormalX=0 NormalY=0 NormalZ=1 AngleXU=0 Radius=3.2
  constraints (192):
    c: Coincident(g0,g1)
    c: Coincident(g1,g2)
    c: Coincident(g2,g3)
    c: Coincident(g3,g0)
    c: Horizontal(g0)
    c: Horizontal(g2)
    c: Vertical(g1)
    c: Vertical(g3)
    c: DistanceX(g0,g0) = 65
    c: DistanceY(g1,g1) = 30
    c: Symmetric(g0,g0,g-2)
    c: Symmetric(g0,g1,g-1)
    c: Coincident(g4,g5)
    c: Coincident(g5,g6)
    c: Coincident(g6,g7)
    c: Coincident(g7,g4)
    c: Horizontal(g4)
    c: Horizontal(g6)
    c: Vertical(g5)
    c: Vertical(g7)
    c: DistanceX(g4,g4) = 58
    c: DistanceY(g5,g5) = 23
    c: Symmetric(g4,g5,g-1)
    c: Symmetric(g4,g4,g-2)
    c: Coincident(g8,g4)
    c: Coincident(g9,g4)
    c: Coincident(g10,g5)
    c: Coincident(g11,g6)
    c: Radius(g11) = 1.375
    c: Radius(g8) = 1.375
    c: Radius(g9) = 1.375
    c: Radius(g10) = 1.375
    c: Coincident(g12,g13)
    c: Coincident(g13,g14)
    c: Coincident(g14,g15)
    c: Coincident(g15,g12)
    c: Horizontal(g12)
    c: Horizontal(g14)
    c: Vertical(g13)
    c: Vertical(g15)
    c: DistanceX(g4,g12) = 0.5
    c: DistanceY(g4,g12) = 0.5
    c: DistanceY(g13,g5) = 0.5
    c: DistanceX(g14,g6) = 0.5
    c: Coincident(g16,g12)
    c: Radius(g16) = 3
    c: Coincident(g17,g12)
    c: Radius(g17) = 3
    c: Coincident(g18,g13)
    c: Radius(g18) = 3
    c: Coincident(g19,g14)
    c: Radius(g19) = 3
    c: PointOnObject(g16,g0)
    c: PointOnObject(g17,g1)
    c: PointOnObject(g18,g2)
    c: PointOnObject(g19,g3)
    c: Coincident(g20,g16)
    c: Horizontal(g20)
    c: Coincident(g20,g17)
    c: Coincident(g21,g17)
    c: Vertical(g21)
    c: Coincident(g18,g21)
    c: Coincident(g22,g18)
    c: Horizontal(g22)
    c: Coincident(g19,g22)
    c: Coincident(g23,g19)
    c: Vertical(g23)
    c: Coincident(g23,g16)
    c: Coincident(g24,g12)
    c: Radius(g24) = 3.3
    c: Coincident(g25,g12)
    c: Radius(g25) = 3.3
    c: Coincident(g26,g13)
    c: Radius(g26) = 3.3
    c: Coincident(g27,g14)
    c: Radius(g27) = 3.3
    c: Vertical(g28)
    c: DistanceX(g28,g2) = 0.3
    c: Coincident(g27,g28)
    c: Coincident(g28,g24)
    c: Horizontal(g29)
    c: DistanceY(g0,g29) = 0.3
    c: Coincident(g24,g29)
    c: Coincident(g25,g29)
    c: Vertical(g30)
    c: DistanceX(g0,g30) = 0.3
    c: Coincident(g25,g30)
    c: Coincident(g30,g26)
    c: Horizontal(g31)
    c: DistanceY(g31,g1) = 0.3
    c: Coincident(g31,g26)
    c: Coincident(g31,g27)
    c: Coincident(g32,g33)
    c: Coincident(g33,g34)
    c: Coincident(g34,g35)
    c: Coincident(g35,g32)
    c: Horizontal(g32)
    c: Horizontal(g34)
    c: Vertical(g33)
    c: Vertical(g35)
    c: DistanceY(g25,g32) = 2
    c: DistanceX(g25,g32) = 2
    c: DistanceY(g33,g26) = 2
    c: DistanceX(g34,g27) = 2
    c: Coincident(g36,g32)
    c: Coincident(g37,g33)
    c: Coincident(g38,g34)
    c: Coincident(g39,g32)
    c: Radius(g39) = 5
    c: Radius(g38) = 5
    c: Radius(g37) = 5
    c: Radius(g36) = 5
    c: Radius(g40) = 3
    c: Tangent(g40,g36)
    c: Tangent(g40,g32)
    c: Tangent(g47,g36)
    c: Radius(g47) = 3
    c: Tangent(g47,g33)
    c: Radius(g46) = 3
    c: Tangent(g46,g37)
    c: Tangent(g46,g33)
    c: Radius(g45) = 3
    c: Tangent(g45,g37)
    c: Tangent(g45,g34)
    c: Radius(g44) = 3
    c: Tangent(g44,g34)
    c: Tangent(g44,g38)
    c: Radius(g43) = 3
    c: Tangent(g43,g38)
    c: Tangent(g43,g35)
    c: Radius(g42) = 3
    c: Tangent(g42,g35)
    c: Tangent(g42,g39)
    c: Radius(g41) = 3
    c: Tangent(g41,g32)
    c: Tangent(g41,g39)
    c: Coincident(g48,g32)
    c: PointOnObject(g48,g36)
    c: Coincident(g49,g40)
    c: PointOnObject(g49,g40)
    c: Coincident(g50,g47)
    c: PointOnObject(g50,g47)
    c: Coincident(g51,g46)
    c: PointOnObject(g51,g46)
    c: Coincident(g52,g33)
    c: PointOnObject(g52,g37)
    c: Coincident(g53,g45)
    c: PointOnObject(g53,g45)
    c: Coincident(g54,g44)
    c: PointOnObject(g54,g44)
    c: Coincident(g55,g34)
    c: PointOnObject(g55,g38)
    c: Coincident(g56,g43)
    c: PointOnObject(g56,g43)
    c: Coincident(g57,g42)
    c: PointOnObject(g57,g42)
    c: Coincident(g58,g32)
    c: PointOnObject(g58,g39)
    c: Coincident(g59,g41)
    c: PointOnObject(g59,g41)
    c: Coincident(g49,g48)
    c: Coincident(g48,g50)
    c: Coincident(g51,g52)
    c: Coincident(g52,g53)
    c: Coincident(g54,g55)
    c: Coincident(g55,g56)
    c: Coincident(g57,g58)
    c: Coincident(g58,g59)
    c: PointOnObject(g60,g32)
    c: Horizontal(g60)
    c: PointOnObject(g61,g33)
    c: Vertical(g61)
    c: PointOnObject(g62,g34)
    c: Horizontal(g62)
    c: PointOnObject(g63,g35)
    c: Vertical(g63)
    c: Coincident(g59,g60)
    c: Coincident(g60,g49)
    c: Coincident(g50,g61)
    c: Coincident(g61,g51)
    c: Coincident(g53,g62)
    c: Coincident(g54,g62)
    c: Coincident(g56,g63)
    c: Coincident(g57,g63)
    c: Coincident(g64,g32)
    c: Coincident(g65,g33)
    c: Coincident(g66,g34)
    c: Coincident(g67,g32)
    c: Radius(g67) = 3.2
    c: Radius(g64) = 3.2
    c: Radius(g65) = 3.2
    c: Radius(g66) = 3.2
FEATURE [PartDesign::Pad] Pad002
  BaseFeature = -> Pad001
  Length = 4
  Length2 = 100
  Profile = -> Sketch004
  Type = 0
FEATURE [Sketcher::SketchObject] Sketch005
  MapMode = 5
  Placement = pos=(0,-17.3,0) rot=(1,0,0;1.5708rad)
  sketch-geometry (22):
    g0: LineSegment StartX=-26.0242 StartY=12 StartZ=0 EndX=-14.2242 EndY=12 EndZ=0
    g1: LineSegment StartX=-14.2242 StartY=12 StartZ=0 EndX=-14.2242 EndY=9.7 EndZ=0
    g2: LineSegment StartX=-26.0242 StartY=9.7 StartZ=0 EndX=-26.0242 EndY=12 EndZ=0
    g3: LineSegment [constr] StartX=-20.1242 StartY=16.7174 StartZ=0 EndX=-20.1242 EndY=2.05389 EndZ=0
    g4: LineSegment [constr] StartX=-26 StartY=7.5 StartZ=0 EndX=23.454 EndY=7.5 EndZ=0
    g5: LineSegment StartX=-24.5941 StartY=8.5 StartZ=0 EndX=-15.6543 EndY=8.5 EndZ=0
    g6: LineSegment StartX=-26.0242 StartY=9.7 StartZ=0 EndX=-24.5941 EndY=8.5 EndZ=0
    g7: LineSegment StartX=-15.6543 StartY=8.5 StartZ=0 EndX=-14.2242 EndY=9.7 EndZ=0
    g8: LineSegment StartX=4.8858 StartY=12 StartZ=0 EndX=12.8858 EndY=12 EndZ=0
    g9: LineSegment StartX=12.8858 StartY=12 StartZ=0 EndX=12.8858 EndY=9.28 EndZ=0
    g10: LineSegment StartX=4.8858 StartY=9.28 StartZ=0 EndX=4.8858 EndY=12 EndZ=0
    g11: LineSegment [constr] StartX=8.8858 StartY=17.7004 StartZ=0 EndX=8.8858 EndY=3.91586 EndZ=0
    g12: LineSegment StartX=4.8858 StartY=9.28 StartZ=0 EndX=5.8858 EndY=8.28 EndZ=0
    g13: LineSegment StartX=11.8858 StartY=8.28 StartZ=0 EndX=12.8858 EndY=9.28 EndZ=0
    g14: LineSegment StartX=5.8858 StartY=8.28 StartZ=0 EndX=11.8858 EndY=8.28 EndZ=0
    g15: LineSegment StartX=17.5058 StartY=12 StartZ=0 EndX=25.5058 EndY=12 EndZ=0
    g16: LineSegment StartX=25.5058 StartY=12 StartZ=0 EndX=25.5058 EndY=9.28 EndZ=0
    g17: LineSegment StartX=17.5058 StartY=9.28 StartZ=0 EndX=17.5058 EndY=12 EndZ=0
    g18: LineSegment StartX=17.5058 StartY=9.28 StartZ=0 EndX=18.5058 EndY=8.28 EndZ=0
    g19: LineSegment StartX=24.5058 StartY=8.28 StartZ=0 EndX=25.5058 EndY=9.28 EndZ=0
    g20: LineSegment StartX=18.5058 StartY=8.28 StartZ=0 EndX=24.5058 EndY=8.28 EndZ=0
    g21: LineSegment [constr] StartX=21.5058 StartY=16.2884 StartZ=0 EndX=21.5058 EndY=2.78996 EndZ=0
  constraints (57):
    c: Coincident(g0,g1)
    c: Coincident(g2,g0)
    c: Horizontal(g0)
    c: Vertical(g1)
    c: Vertical(g2)
    c: Vertical(g3)
    c: Symmetric(g0,g0,g3)
    c: DistanceX(g0,g0) = 11.8
    c: Horizontal(g4)
    c: Horizontal(g5)
    c: Angle(g5,g6) = 2.44346
    c: Angle(g7,g5) = 2.44346
    c: Coincident(g2,g6)
    c: Coincident(g6,g5)
    c: DistanceY(g5,g2) = 1.2
    c: Coincident(g7,g5)
    c: DistanceY(g5,g7) = 1.2
    c: Coincident(g1,g7)
    c: DistanceY(g4,g5) = 1
    c: Coincident(g8,g9)
    c: Coincident(g10,g8)
    c: Horizontal(g8)
    c: Vertical(g9)
    c: Vertical(g10)
    c: DistanceX(g8,g8) = 8
    c: Vertical(g11)
    c: DistanceX(g3,g11) = 29.01
    c: Symmetric(g8,g8,g11)
    c: Horizontal(g14)
    c: DistanceY(g4,g14) = 0.78
    c: Angle(g13,g14) = 2.35619
    c: Angle(g14,g12) = 2.35619
    c: Coincident(g12,g14)
    c: Coincident(g12,g10)
    c: DistanceY(g12,g10) = 1
    c: Coincident(g14,g13)
    c: Coincident(g13,g9)
    c: DistanceY(g13,g9) = 1
    c: Coincident(g15,g16)
    c: Coincident(g17,g15)
    c: Horizontal(g15)
    c: Vertical(g16)
    c: Vertical(g17)
    c: Equal(g8,g15) = 7.8
    c: Horizontal(g20)
    c: Angle(g19,g20) = 2.35619
    c: Angle(g20,g18) = 2.35619
    c: Coincident(g18,g20)
    c: Coincident(g18,g17)
    c: DistanceY(g18,g17) = 1
    c: Coincident(g20,g19)
    c: Coincident(g19,g16)
    c: DistanceY(g19,g16) = 1
    c: DistanceY(g4,g18) = 0.78
    c: Vertical(g21)
    c: DistanceX(g11,g21) = 12.62
    c: Symmetric(g15,g15,g21)
FEATURE [PartDesign::Pocket] Pocket002
  BaseFeature = -> Pad002
  Length = 5
  Length2 = 100
  Profile = -> Sketch005
  Type = 2
FEATURE [Sketcher::SketchObject] Sketch006
  ExternalGeometry = -> [Pocket002]
  MapMode = 5
  Placement = pos=(-34.8,0,0) rot=(0.57735,-0.57735,-0.57735;2.0944rad)
  Support = -> [Pocket002]
  sketch-geometry (12):
    g0: LineSegment [constr] StartX=-8.50001 StartY=7.5 StartZ=0 EndX=0.928937 EndY=7.5 EndZ=0
    g1: LineSegment [constr] StartX=-1.67421 StartY=13.4438 StartZ=0 EndX=-1.67421 EndY=3.80207 EndZ=0
    g2: LineSegment [constr] StartX=-11.4942 StartY=7.5 StartZ=0 EndX=-11.4942 EndY=14.033 EndZ=0
    g3: LineSegment StartX=4.62579 StartY=10.3 StartZ=0 EndX=4.62579 EndY=8.5 EndZ=0
    g4: LineSegment StartX=4.62579 StartY=8.5 StartZ=0 EndX=-7.97421 EndY=8.5 EndZ=0
    g5: LineSegment StartX=-7.97421 StartY=8.5 StartZ=0 EndX=-7.97421 EndY=10.3 EndZ=0
    g6: LineSegment [constr] StartX=4.62579 StartY=10.3 StartZ=0 EndX=-7.97421 EndY=10.3 EndZ=0
    g7: ArcOfEllipse CenterX=-1.67421 CenterY=10.3 CenterZ=0 NormalX=0 NormalY=0 NormalZ=1 MajorRadius=6.3 MinorRadius=1.00676 AngleXU=3.14159 StartAngle=3.14159 EndAngle=6.28319
    g8: LineSegment [constr] StartX=-7.97421 StartY=10.3 StartZ=0 EndX=4.62579 EndY=10.3 EndZ=0
    g9: LineSegment [constr] StartX=-1.67421 StartY=9.29324 StartZ=0 EndX=-1.67421 EndY=11.3068 EndZ=0
    g10: GeomPoint X=-7.89325 Y=10.3 Z=0
    g11: GeomPoint X=4.54482 Y=10.3 Z=0
FEATURE [PartDesign::Pocket] Pocket003
  BaseFeature = -> Pocket002
  Length = 5
  Length2 = 100
  Profile = -> Sketch006
  Type = 2
FEATURE [PartDesign::Chamfer] Chamfer
  Base = -> Pocket003 [Edge60,Edge62]
  BaseFeature = -> Pocket003
  Size = 0.6
FEATURE [Sketcher::SketchObject] Sketch007
  ExternalGeometry = -> [Chamfer]
  MapMode = 5
  Placement = pos=(0,0,16) rot=(0,0,1;0rad)
  Support = -> [Chamfer]
  sketch-geometry (4):
    g0: Circle CenterX=34.8 CenterY=17.3 CenterZ=0 NormalX=0 NormalY=0 NormalZ=1 AngleXU=0 Radius=2.43827
    g1: Circle CenterX=-34.8 CenterY=17.3 CenterZ=0 NormalX=0 NormalY=0 NormalZ=1 AngleXU=0 Radius=2.44385
    g2: Circle CenterX=-34.8 CenterY=-17.3 CenterZ=0 NormalX=0 NormalY=0 NormalZ=1 AngleXU=0 Radius=2.67402
    g3: Circle CenterX=34.8 CenterY=-17.3 CenterZ=0 NormalX=0 NormalY=0 NormalZ=1 AngleXU=0 Radius=2.67742
  constraints (4):
    c: Coincident(g0,g-3)
    c: Coincident(g1,g-4)
    c: Coincident(g2,g-6)
    c: Coincident(g3,g-5)
FEATURE [PartDesign::Hole] Hole
  BaseFeature = -> Chamfer
  Depth = 25
  DepthType = 1
  Diameter = 3.3
  DrillPoint = 1
  DrillPointAngle = 118
  HoleCutCountersinkAngle = 90
  HoleCutDepth = 0
  HoleCutDiameter = 3
  HoleCutType = 0
  ModelActualThread = false
  Profile = -> Sketch007
  Tapered = false
  TaperedAngle = 90
  ThreadAngle = 0
  ThreadClass = 0
  ThreadCutOffInner = 0
  ThreadCutOffOuter = 0
  ThreadDirection = 0
  ThreadFit = 0
  ThreadPitch = 0
  ThreadSize = 3
  ThreadType = 1
  Threaded = false
FEATURE [Sketcher::SketchObject] Sketch008
  ExternalGeometry = -> [Hole]
  MapMode = 5
  Placement = pos=(0,0,0) rot=(1,0,0;3.14159rad)
  Support = -> [Hole]
  sketch-geometry (32):
    g0: LineSegment [constr] StartX=-34.8 StartY=27.181 StartZ=0 EndX=-34.8 EndY=-26.8986 EndZ=0
    g1: LineSegment [constr] StartX=34.8 StartY=-24.6336 StartZ=0 EndX=34.8 EndY=23.8401 EndZ=0
    g2: LineSegment [constr] StartX=-45.3318 StartY=17.3 StartZ=0 EndX=42.1188 EndY=17.3 EndZ=0
    g3: LineSegment [constr] StartX=-44.7382 StartY=-17.3 StartZ=0 EndX=39.4916 EndY=-17.3 EndZ=0
    g4: LineSegment StartX=34.8 StartY=14.1708 StartZ=0 EndX=37.51 EndY=15.7354 EndZ=0
    g5: LineSegment StartX=37.51 StartY=15.7354 StartZ=0 EndX=37.51 EndY=18.8646 EndZ=0
    g6: LineSegment StartX=37.51 StartY=18.8646 StartZ=0 EndX=34.8 EndY=20.4292 EndZ=0
    g7: LineSegment StartX=34.8 StartY=20.4292 StartZ=0 EndX=32.09 EndY=18.8646 EndZ=0
    g8: LineSegment StartX=32.09 StartY=18.8646 StartZ=0 EndX=32.09 EndY=15.7354 EndZ=0
    g9: LineSegment StartX=32.09 StartY=15.7354 StartZ=0 EndX=34.8 EndY=14.1708 EndZ=0
    g10: Circle [constr] CenterX=34.8 CenterY=17.3 CenterZ=0 NormalX=0 NormalY=0 NormalZ=1 AngleXU=0 Radius=3.12924
    g11: LineSegment StartX=-34.8 StartY=14.1708 StartZ=0 EndX=-32.09 EndY=15.7354 EndZ=0
    g12: LineSegment StartX=-32.09 StartY=15.7354 StartZ=0 EndX=-32.09 EndY=18.8646 EndZ=0
    g13: LineSegment StartX=-32.09 StartY=18.8646 StartZ=0 EndX=-34.8 EndY=20.4292 EndZ=0
    g14: LineSegment StartX=-34.8 StartY=20.4292 StartZ=0 EndX=-37.51 EndY=18.8646 EndZ=0
    g15: LineSegment StartX=-37.51 StartY=18.8646 StartZ=0 EndX=-37.51 EndY=15.7354 EndZ=0
    g16: LineSegment StartX=-37.51 StartY=15.7354 StartZ=0 EndX=-34.8 EndY=14.1708 EndZ=0
    g17: Circle [constr] CenterX=-34.8 CenterY=17.3 CenterZ=0 NormalX=0 NormalY=0 NormalZ=1 AngleXU=0 Radius=3.12924
    g18: LineSegment StartX=34.8 StartY=-20.4292 StartZ=0 EndX=37.51 EndY=-18.8646 EndZ=0
    g19: LineSegment StartX=37.51 StartY=-18.8646 StartZ=0 EndX=37.51 EndY=-15.7354 EndZ=0
    g20: LineSegment StartX=37.51 StartY=-15.7354 StartZ=0 EndX=34.8 EndY=-14.1708 EndZ=0
    g21: LineSegment StartX=34.8 StartY=-14.1708 StartZ=0 EndX=32.09 EndY=-15.7354 EndZ=0
    g22: LineSegment StartX=32.09 StartY=-15.7354 StartZ=0 EndX=32.09 EndY=-18.8646 EndZ=0
    g23: LineSegment StartX=32.09 StartY=-18.8646 StartZ=0 EndX=34.8 EndY=-20.4292 EndZ=0
    g24: Circle [constr] CenterX=34.8 CenterY=-17.3 CenterZ=0 NormalX=0 NormalY=0 NormalZ=1 AngleXU=0 Radius=3.12924
    g25: LineSegment StartX=-34.8 StartY=-20.4292 StartZ=0 EndX=-32.09 EndY=-18.8646 EndZ=0
    g26: LineSegment StartX=-32.09 StartY=-18.8646 StartZ=0 EndX=-32.09 EndY=-15.7354 EndZ=0
    g27: LineSegment StartX=-32.09 StartY=-15.7354 StartZ=0 EndX=-34.8 EndY=-14.1708 EndZ=0
    g28: LineSegment StartX=-34.8 StartY=-14.1708 StartZ=0 EndX=-37.51 EndY=-15.7354 EndZ=0
    g29: LineSegment StartX=-37.51 StartY=-15.7354 StartZ=0 EndX=-37.51 EndY=-18.8646 EndZ=0
    g30: LineSegment StartX=-37.51 StartY=-18.8646 StartZ=0 EndX=-34.8 EndY=-20.4292 EndZ=0
    g31: Circle [constr] CenterX=-34.8 CenterY=-17.3 CenterZ=0 NormalX=0 NormalY=0 NormalZ=1 AngleXU=0 Radius=3.12924
  constraints (72):
    c: Vertical(g0)
    c: Vertical(g1)
    c: Horizontal(g2)
    c: Horizontal(g3)
    c: PointOnObject(g-6,g3)
    c: PointOnObject(g-6,g1)
    c: PointOnObject(g-5,g0)
    c: PointOnObject(g-4,g2)
    c: Coincident(g4,g5)
    c: Coincident(g5,g6)
    c: Coincident(g6,g7)
    c: Coincident(g7,g8)
    c: Coincident(g8,g9)
    c: Coincident(g9,g4)
    c: Equal(g4, g5-g9) x5
    c: PointOnObject(g4,g10)
    c: PointOnObject(g5,g10)
    c: PointOnObject(g6,g10)
    c: PointOnObject(g7,g10)
    c: PointOnObject(g8,g10)
    c: PointOnObject(g9,g10)
    c: Coincident(g10,g-3)
    c: PointOnObject(g9,g1)
    c: DistanceX(g7,g5) = 5.42
    c: Coincident(g11,g12)
    c: Coincident(g12,g13)
    c: Coincident(g13,g14)
    c: Coincident(g14,g15)
    c: Coincident(g15,g16)
    c: Coincident(g16,g11)
    c: Equal(g11, g12-g16) x5
    c: PointOnObject(g11,g17)
    c: PointOnObject(g12,g17)
    c: PointOnObject(g13,g17)
    c: PointOnObject(g14,g17)
    c: PointOnObject(g15,g17)
    c: PointOnObject(g16,g17)
    c: Coincident(g17,g-4)
    c: PointOnObject(g16,g0)
    c: DistanceX(g14,g12) = 5.42
    c: Coincident(g18,g19)
    c: Coincident(g19,g20)
    c: Coincident(g20,g21)
    c: Coincident(g21,g22)
    c: Coincident(g22,g23)
    c: Coincident(g23,g18)
    c: Equal(g18, g19-g23) x5
    c: PointOnObject(g18,g24)
    c: PointOnObject(g19,g24)
    c: PointOnObject(g20,g24)
    c: PointOnObject(g21,g24)
    c: PointOnObject(g22,g24)
    c: PointOnObject(g23,g24)
    c: Coincident(g24,g-6)
    c: PointOnObject(g23,g1)
    c: DistanceX(g21,g19) = 5.42
    c: Coincident(g25,g26)
    c: Coincident(g26,g27)
    c: Coincident(g27,g28)
    c: Coincident(g28,g29)
    c: Coincident(g29,g30)
    c: Coincident(g30,g25)
    c: Equal(g25, g26-g30) x5
    c: PointOnObject(g25,g31)
    c: PointOnObject(g26,g31)
    c: PointOnObject(g27,g31)
    c: PointOnObject(g28,g31)
    c: PointOnObject(g29,g31)
    c: PointOnObject(g30,g31)
    c: PointOnObject(g30,g0)
    c: DistanceX(g28,g26) = 5.42
    c: Coincident(g31,g-5)
FEATURE [PartDesign::Pocket] Pocket004
  BaseFeature = -> Hole
  Length = 8
  Length2 = 100
  Profile = -> Sketch008
  Type = 0
FEATURE [Sketcher::SketchObject] Sketch009
  MapMode = 5
  Placement = pos=(0,0,7.5) rot=(0,0,1;0rad)
  Support = -> [Pocket004]
  expr: Constraints[51] = Sketch.Constraints[51]
  expr: Constraints[49] = Sketch.Constraints[49]
  expr: Constraints[47] = Sketch.Constraints[47]
  expr: Constraints[40] = Sketch.Constraints[40]
  expr: Constraints[31] = Sketch.Constraints[31]
  expr: Constraints[30] = Sketch.Constraints[30]
  expr: Constraints[29] = Sketch.Constraints[29]
  expr: Constraints[28] = Sketch.Constraints[28]
  expr: Constraints[21] = Sketch.Constraints[21]
  expr: Constraints[20] = Sketch.Constraints[20]
  expr: Constraints[45] = Sketch.Constraints[45]
  expr: Constraints[43] = Sketch.Constraints[43]
  expr: Constraints[42] = Sketch.Constraints[42]
  expr: Constraints[41] = Sketch.Constraints[41]
  expr: Constraints[9] = Sketch.Constraints[9]
  expr: Constraints[8] = Sketch.Constraints[8]
  sketch-geometry (28):
    g0: LineSegment [constr] StartX=-32.5 StartY=15 StartZ=0 EndX=32.5 EndY=15 EndZ=0
    g1: LineSegment [constr] StartX=32.5 StartY=15 StartZ=0 EndX=32.5 EndY=-15 EndZ=0
    g2: LineSegment [constr] StartX=32.5 StartY=-15 StartZ=0 EndX=-32.5 EndY=-15 EndZ=0
    g3: LineSegment [constr] StartX=-32.5 StartY=-15 StartZ=0 EndX=-32.5 EndY=15 EndZ=0
    g4: LineSegment [constr] StartX=-29 StartY=11.5 StartZ=0 EndX=29 EndY=11.5 EndZ=0
    g5: LineSegment [constr] StartX=29 StartY=11.5 StartZ=0 EndX=29 EndY=-11.5 EndZ=0
    g6: LineSegment [constr] StartX=29 StartY=-11.5 StartZ=0 EndX=-29 EndY=-11.5 EndZ=0
    g7: LineSegment [constr] StartX=-29 StartY=-11.5 StartZ=0 EndX=-29 EndY=11.5 EndZ=0
    g8: Circle [constr] CenterX=-29 CenterY=11.5 CenterZ=0 NormalX=0 NormalY=0 NormalZ=1 AngleXU=0 Radius=1.375
    g9: Circle [constr] CenterX=29 CenterY=11.5 CenterZ=0 NormalX=0 NormalY=0 NormalZ=1 AngleXU=0 Radius=1.375
    g10: Circle [constr] CenterX=29 CenterY=-11.5 CenterZ=0 NormalX=0 NormalY=0 NormalZ=1 AngleXU=0 Radius=1.375
    g11: Circle [constr] CenterX=-29 CenterY=-11.5 CenterZ=0 NormalX=0 NormalY=0 NormalZ=1 AngleXU=0 Radius=1.375
    g12: LineSegment [constr] StartX=-29.5 StartY=12 StartZ=0 EndX=29.5 EndY=12 EndZ=0
    g13: LineSegment [constr] StartX=29.5 StartY=12 StartZ=0 EndX=29.5 EndY=-12 EndZ=0
    g14: LineSegment [constr] StartX=29.5 StartY=-12 StartZ=0 EndX=-29.5 EndY=-12 EndZ=0
    g15: LineSegment [constr] StartX=-29.5 StartY=-12 StartZ=0 EndX=-29.5 EndY=12 EndZ=0
    g16: ArcOfCircle [constr] CenterX=-29.5 CenterY=12 CenterZ=0 NormalX=0 NormalY=0 NormalZ=1 AngleXU=0 Radius=3 StartAngle=1.5708 EndAngle=3.14159
    g17: ArcOfCircle [constr] CenterX=29.5 CenterY=12 CenterZ=0 NormalX=0 NormalY=0 NormalZ=1 AngleXU=0 Radius=3 StartAngle=3.7568e-08 EndAngle=1.5708
    g18: ArcOfCircle [constr] CenterX=29.5 CenterY=-12 CenterZ=0 NormalX=0 NormalY=0 NormalZ=1 AngleXU=0 Radius=3 StartAngle=4.71239 EndAngle=6.28319
    g19: ArcOfCircle [constr] CenterX=-29.5 CenterY=-12 CenterZ=0 NormalX=0 NormalY=0 NormalZ=1 AngleXU=0 Radius=3 StartAngle=3.14159 EndAngle=4.71239
    g20: LineSegment [constr] StartX=-29.5 StartY=15 StartZ=0 EndX=29.5 EndY=15 EndZ=0
    g21: LineSegment [constr] StartX=32.5 StartY=12 StartZ=0 EndX=32.5 EndY=-12 EndZ=0
    g22: LineSegment [constr] StartX=29.5 StartY=-15 StartZ=0 EndX=-29.5 EndY=-15 EndZ=0
    g23: LineSegment [constr] StartX=-32.5 StartY=-12 StartZ=0 EndX=-32.5 EndY=12 EndZ=0
    g24: Circle CenterX=-29 CenterY=-11.5 CenterZ=0 NormalX=0 NormalY=0 NormalZ=1 AngleXU=0 Radius=1.07106
    g25: Circle CenterX=29 CenterY=-11.5 CenterZ=0 NormalX=0 NormalY=0 NormalZ=1 AngleXU=0 Radius=1.09378
    g26: Circle CenterX=29 CenterY=11.5 CenterZ=0 NormalX=0 NormalY=0 NormalZ=1 AngleXU=0 Radius=1.14533
    g27: Circle CenterX=-29 CenterY=11.5 CenterZ=0 NormalX=0 NormalY=0 NormalZ=1 AngleXU=0 Radius=1.23522
  constraints (72):
    c: Coincident(g0,g1)
    c: Coincident(g1,g2)
    c: Coincident(g2,g3)
    c: Coincident(g3,g0)
    c: Horizontal(g0)
    c: Horizontal(g2)
    c: Vertical(g1)
    c: Vertical(g3)
    c: DistanceX(g0,g0) = 65
    c: DistanceY(g1,g1) = 30
    c: Symmetric(g0,g0,g-2)
    c: Symmetric(g0,g1,g-1)
    c: Coincident(g4,g5)
    c: Coincident(g5,g6)
    c: Coincident(g6,g7)
    c: Coincident(g7,g4)
    c: Horizontal(g4)
    c: Horizontal(g6)
    c: Vertical(g5)
    c: Vertical(g7)
    c: DistanceX(g4,g4) = 58
    c: DistanceY(g5,g5) = 23
    c: Symmetric(g4,g5,g-1)
    c: Symmetric(g4,g4,g-2)
    c: Coincident(g8,g4)
    c: Coincident(g9,g4)
    c: Coincident(g10,g5)
    c: Coincident(g11,g6)
    c: Radius(g11) = 1.375
    c: Radius(g8) = 1.375
    c: Radius(g9) = 1.375
    c: Radius(g10) = 1.375
    c: Coincident(g12,g13)
    c: Coincident(g13,g14)
    c: Coincident(g14,g15)
    c: Coincident(g15,g12)
    c: Horizontal(g12)
    c: Horizontal(g14)
    c: Vertical(g13)
    c: Vertical(g15)
    c: DistanceX(g4,g12) = 0.5
    c: DistanceY(g4,g12) = 0.5
    c: DistanceY(g13,g5) = 0.5
    c: DistanceX(g14,g6) = 0.5
    c: Coincident(g16,g12)
    c: Radius(g16) = 3
    c: Coincident(g17,g12)
    c: Radius(g17) = 3
    c: Coincident(g18,g13)
    c: Radius(g18) = 3
    c: Coincident(g19,g14)
    c: Radius(g19) = 3
    c: PointOnObject(g16,g0)
    c: PointOnObject(g17,g1)
    c: PointOnObject(g18,g2)
    c: PointOnObject(g19,g3)
    c: Coincident(g20,g16)
    c: Horizontal(g20)
    c: Coincident(g20,g17)
    c: Coincident(g21,g17)
    c: Vertical(g21)
    c: Coincident(g18,g21)
    c: Coincident(g22,g18)
    c: Horizontal(g22)
    c: Coincident(g19,g22)
    c: Coincident(g23,g19)
    c: Vertical(g23)
    c: Coincident(g23,g16)
    c: Coincident(g24,g6)
    c: Coincident(g25,g5)
    c: Coincident(g26,g4)
    c: Coincident(g27,g4)
FEATURE [PartDesign::Hole] Hole001
  BaseFeature = -> Pocket004
  Depth = 25
  DepthType = 1
  Diameter = 2.2
  DrillPoint = 1
  DrillPointAngle = 118
  HoleCutCountersinkAngle = 90
  HoleCutDepth = 0
  HoleCutDiameter = 2
  HoleCutType = 0
  ModelActualThread = false
  Profile = -> Sketch009
  Tapered = false
  TaperedAngle = 90
  ThreadAngle = 60
  ThreadClass = 0
  ThreadCutOffInner = 0.0433013
  ThreadCutOffOuter = 0.0866025
  ThreadDirection = 0
  ThreadFit = 0
  ThreadPitch = 0.4
  ThreadSize = 1
  ThreadType = 1
  Threaded = false
FEATURE [Sketcher::SketchObject] Sketch010
  ExternalGeometry = -> [Hole001]
  MapMode = 5
  Placement = pos=(0,0,0) rot=(1,0,0;3.14159rad)
  Support = -> [Hole001]
  sketch-geometry (32):
    g0: LineSegment [constr] StartX=-29 StartY=20.1024 StartZ=0 EndX=-29 EndY=-21.8008 EndZ=0
    g1: LineSegment [constr] StartX=29 StartY=21.2945 StartZ=0 EndX=29 EndY=-21.3239 EndZ=0
    g2: LineSegment [constr] StartX=-40.5495 StartY=-11.5 StartZ=0 EndX=38.5479 EndY=-11.5 EndZ=0
    g3: LineSegment [constr] StartX=-40.9667 StartY=11.5 StartZ=0 EndX=41.409 EndY=11.5 EndZ=0
    g4: LineSegment StartX=29 StartY=9.13286 StartZ=0 EndX=31.05 EndY=10.3164 EndZ=0
    g5: LineSegment StartX=31.05 StartY=10.3164 StartZ=0 EndX=31.05 EndY=12.6836 EndZ=0
    g6: LineSegment StartX=31.05 StartY=12.6836 StartZ=0 EndX=29 EndY=13.8671 EndZ=0
    g7: LineSegment StartX=29 StartY=13.8671 StartZ=0 EndX=26.95 EndY=12.6836 EndZ=0
    g8: LineSegment StartX=26.95 StartY=12.6836 StartZ=0 EndX=26.95 EndY=10.3164 EndZ=0
    g9: LineSegment StartX=26.95 StartY=10.3164 StartZ=0 EndX=29 EndY=9.13286 EndZ=0
    g10: Circle [constr] CenterX=29 CenterY=11.5 CenterZ=0 NormalX=0 NormalY=0 NormalZ=1 AngleXU=0 Radius=2.36714
    g11: LineSegment StartX=-29 StartY=9.13286 StartZ=0 EndX=-26.95 EndY=10.3164 EndZ=0
    g12: LineSegment StartX=-26.95 StartY=10.3164 StartZ=0 EndX=-26.95 EndY=12.6836 EndZ=0
    g13: LineSegment StartX=-26.95 StartY=12.6836 StartZ=0 EndX=-29 EndY=13.8671 EndZ=0
    g14: LineSegment StartX=-29 StartY=13.8671 StartZ=0 EndX=-31.05 EndY=12.6836 EndZ=0
    g15: LineSegment StartX=-31.05 StartY=12.6836 StartZ=0 EndX=-31.05 EndY=10.3164 EndZ=0
    g16: LineSegment StartX=-31.05 StartY=10.3164 StartZ=0 EndX=-29 EndY=9.13286 EndZ=0
    g17: Circle [constr] CenterX=-29 CenterY=11.5 CenterZ=0 NormalX=0 NormalY=0 NormalZ=1 AngleXU=0 Radius=2.36714
    g18: LineSegment StartX=-29 StartY=-13.8671 StartZ=0 EndX=-26.95 EndY=-12.6836 EndZ=0
    g19: LineSegment StartX=-26.95 StartY=-12.6836 StartZ=0 EndX=-26.95 EndY=-10.3164 EndZ=0
    g20: LineSegment StartX=-26.95 StartY=-10.3164 StartZ=0 EndX=-29 EndY=-9.13286 EndZ=0
    g21: LineSegment StartX=-29 StartY=-9.13286 StartZ=0 EndX=-31.05 EndY=-10.3164 EndZ=0
    g22: LineSegment StartX=-31.05 StartY=-10.3164 StartZ=0 EndX=-31.05 EndY=-12.6836 EndZ=0
    g23: LineSegment StartX=-31.05 StartY=-12.6836 StartZ=0 EndX=-29 EndY=-13.8671 EndZ=0
    g24: Circle [constr] CenterX=-29 CenterY=-11.5 CenterZ=0 NormalX=0 NormalY=0 NormalZ=1 AngleXU=0 Radius=2.36714
    g25: LineSegment StartX=29 StartY=-13.8671 StartZ=0 EndX=31.05 EndY=-12.6836 EndZ=0
    g26: LineSegment StartX=31.05 StartY=-12.6836 StartZ=0 EndX=31.05 EndY=-10.3164 EndZ=0
    g27: LineSegment StartX=31.05 StartY=-10.3164 StartZ=0 EndX=29 EndY=-9.13286 EndZ=0
    g28: LineSegment StartX=29 StartY=-9.13286 StartZ=0 EndX=26.95 EndY=-10.3164 EndZ=0
    g29: LineSegment StartX=26.95 StartY=-10.3164 StartZ=0 EndX=26.95 EndY=-12.6836 EndZ=0
    g30: LineSegment StartX=26.95 StartY=-12.6836 StartZ=0 EndX=29 EndY=-13.8671 EndZ=0
    g31: Circle [constr] CenterX=29 CenterY=-11.5 CenterZ=0 NormalX=0 NormalY=0 NormalZ=1 AngleXU=0 Radius=2.36714
  constraints (72):
    c: Vertical(g0)
    c: Vertical(g1)
    c: Horizontal(g2)
    c: Horizontal(g3)
    c: PointOnObject(g-3,g3)
    c: PointOnObject(g-6,g2)
    c: PointOnObject(g-6,g1)
    c: PointOnObject(g-5,g0)
    c: Coincident(g4,g5)
    c: Coincident(g5,g6)
    c: Coincident(g6,g7)
    c: Coincident(g7,g8)
    c: Coincident(g8,g9)
    c: Coincident(g9,g4)
    c: Equal(g4, g5-g9) x5
    c: PointOnObject(g4,g10)
    c: PointOnObject(g5,g10)
    c: PointOnObject(g6,g10)
    c: PointOnObject(g7,g10)
    c: PointOnObject(g8,g10)
    c: PointOnObject(g9,g10)
    c: Coincident(g10,g-3)
    c: PointOnObject(g9,g1)
    c: DistanceX(g7,g5) = 4.1
    c: Coincident(g11,g12)
    c: Coincident(g12,g13)
    c: Coincident(g13,g14)
    c: Coincident(g14,g15)
    c: Coincident(g15,g16)
    c: Coincident(g16,g11)
    c: Equal(g11, g12-g16) x5
    c: PointOnObject(g11,g17)
    c: PointOnObject(g12,g17)
    c: PointOnObject(g13,g17)
    c: PointOnObject(g14,g17)
    c: PointOnObject(g15,g17)
    c: PointOnObject(g16,g17)
    c: Coincident(g17,g-4)
    c: PointOnObject(g16,g0)
    c: DistanceX(g14,g12) = 4.1
    c: Coincident(g18,g19)
    c: Coincident(g19,g20)
    c: Coincident(g20,g21)
    c: Coincident(g21,g22)
    c: Coincident(g22,g23)
    c: Coincident(g23,g18)
    c: Equal(g18, g19-g23) x5
    c: PointOnObject(g18,g24)
    c: PointOnObject(g19,g24)
    c: PointOnObject(g20,g24)
    c: PointOnObject(g21,g24)
    c: PointOnObject(g22,g24)
    c: PointOnObject(g23,g24)
    c: Coincident(g24,g-5)
    c: PointOnObject(g23,g0)
    c: DistanceX(g21,g19) = 4.1
    c: Coincident(g25,g26)
    c: Coincident(g26,g27)
    c: Coincident(g27,g28)
    c: Coincident(g28,g29)
    c: Coincident(g29,g30)
    c: Coincident(g30,g25)
    c: Equal(g25, g26-g30) x5
    c: PointOnObject(g25,g31)
    c: PointOnObject(g26,g31)
    c: PointOnObject(g27,g31)
    c: PointOnObject(g28,g31)
    c: PointOnObject(g29,g31)
    c: PointOnObject(g30,g31)
    c: Coincident(g31,g-6)
    c: PointOnObject(g30,g1)
    c: DistanceX(g28,g26) = 4.1
FEATURE [PartDesign::Pocket] Pocket005
  BaseFeature = -> Hole001
  Length = 4.5
  Length2 = 100
  Profile = -> Sketch010
  Type = 0
FEATURE [PartDesign::Fillet] Fillet
  Base = -> Pocket005 [Edge312,Edge306,Edge310,Edge308]
  BaseFeature = -> Pocket005
  Radius = 0.6
FEATURE [Sketcher::SketchObject] Sketch011
  ExternalGeometry = -> [Fillet]
  MapMode = 5
  Placement = pos=(32.8,0,0) rot=(0.57735,-0.57735,-0.57735;2.0944rad)
  Support = -> [Fillet]
  sketch-geometry (6):
    g0: LineSegment [constr] StartX=8.50001 StartY=7.5 StartZ=0 EndX=-8.09097 EndY=7.5 EndZ=0
    g1: LineSegment StartX=-9.5 StartY=12 StartZ=0 EndX=9.5 EndY=12 EndZ=0
    g2: LineSegment StartX=9.5 StartY=12 StartZ=0 EndX=9.5 EndY=8.5 EndZ=0
    g3: LineSegment StartX=9.5 StartY=8.5 StartZ=0 EndX=-9.5 EndY=8.5 EndZ=0
    g4: LineSegment StartX=-9.5 StartY=8.5 StartZ=0 EndX=-9.5 EndY=12 EndZ=0
    g5: LineSegment [constr] StartX=0 StartY=15.3767 StartZ=0 EndX=0 EndY=2.68391 EndZ=0
  constraints (16):
    c: Coincident(g0,g-3)
    c: Horizontal(g0)
    c: Coincident(g1,g2)
    c: Coincident(g2,g3)
    c: Coincident(g3,g4)
    c: Coincident(g4,g1)
    c: Horizontal(g1)
    c: Horizontal(g3)
    c: Vertical(g2)
    c: Vertical(g4)
    c: DistanceX(g1,g1) = 19
    c: PointOnObject(g5,g-2)
    c: Vertical(g5)
    c: Symmetric(g1,g1,g5)
    c: PointOnObject(g1,g-4)
    c: DistanceY(g0,g2) = 1
FEATURE [PartDesign::Pocket] Pocket006
  BaseFeature = -> Fillet
  Length = 0.7
  Length2 = 100
  Profile = -> Sketch011
  Type = 0
FEATURE [Sketcher::SketchObject] Sketch012
  ExternalGeometry = -> [Pocket006]
  MapMode = 5
  Placement = pos=(-32.8,0,0) rot=(0.57735,0.57735,0.57735;2.0944rad)
  Support = -> [Pocket006]
  sketch-geometry (15):
    g0: LineSegment [constr] StartX=8.97421 StartY=12 StartZ=0 EndX=8.97421 EndY=4.11024 EndZ=0
    g1: LineSegment [constr] StartX=-5.62579 StartY=12 StartZ=0 EndX=-5.62579 EndY=3.6342 EndZ=0
    g2: LineSegment [constr] StartX=-5.62579 StartY=12 StartZ=0 EndX=8.97421 EndY=12 EndZ=0
    g3: LineSegment [constr] StartX=8.17421 StartY=9.09588 StartZ=0 EndX=8.17421 EndY=3.57816 EndZ=0
    g4: LineSegment [constr] StartX=-4.72579 StartY=9.58242 StartZ=0 EndX=-4.72579 EndY=4.4197 EndZ=0
    g5: LineSegment [constr] StartX=-8.15183 StartY=11.2 StartZ=0 EndX=11.8659 EndY=11.2 EndZ=0
    g6: LineSegment [constr] StartX=-6.90186 StartY=10.9 StartZ=0 EndX=10.8983 EndY=10.9 EndZ=0
    g7: LineSegment StartX=-5.62579 StartY=12 StartZ=0 EndX=-1.62579 EndY=12 EndZ=0
    g8: LineSegment StartX=-1.62579 StartY=12 StartZ=0 EndX=-1.62579 EndY=10.9 EndZ=0
    g9: LineSegment StartX=-1.62579 StartY=10.9 StartZ=0 EndX=-5.62579 EndY=10.9 EndZ=0
    g10: LineSegment StartX=-5.62579 StartY=10.9 StartZ=0 EndX=-5.62579 EndY=12 EndZ=0
    g11: LineSegment StartX=8.97421 StartY=12 StartZ=0 EndX=4.97421 EndY=12 EndZ=0
    g12: LineSegment StartX=4.97421 StartY=12 StartZ=0 EndX=4.97421 EndY=10.9 EndZ=0
    g13: LineSegment StartX=4.97421 StartY=10.9 StartZ=0 EndX=8.97421 EndY=10.9 EndZ=0
    g14: LineSegment StartX=8.97421 StartY=10.9 StartZ=0 EndX=8.97421 EndY=12 EndZ=0
  constraints (38):
    c: Vertical(g0)
    c: DistanceX(g-4,g0) = 1
    c: Vertical(g1)
    c: DistanceX(g1,g-5) = 1
    c: PointOnObject(g2,g-7)
    c: Horizontal(g2)
    c: Vertical(g3)
    c: DistanceX(g3,g0) = 0.8
    c: Vertical(g4)
    c: DistanceX(g1,g4) = 0.9
    c: Horizontal(g5)
    c: DistanceY(g5,g2) = 0.8
    c: Horizontal(g6)
    c: DistanceY(g6,g-7) = 1.1
    c: Coincident(g1,g2)
    c: Coincident(g2,g0)
    c: Coincident(g7,g8)
    c: Coincident(g8,g9)
    c: Coincident(g9,g10)
    c: Coincident(g10,g7)
    c: Horizontal(g7)
    c: Horizontal(g9)
    c: Vertical(g8)
    c: Vertical(g10)
    c: Coincident(g7,g1)
    c: PointOnObject(g8,g6)
    c: Coincident(g11,g12)
    c: Coincident(g12,g13)
    c: Coincident(g13,g14)
    c: Coincident(g14,g11)
    c: Horizontal(g11)
    c: Horizontal(g13)
    c: Vertical(g12)
    c: Vertical(g14)
    c: Coincident(g11,g0)
    c: PointOnObject(g12,g6)
    c: DistanceX(g7,g7) = 4
    c: DistanceX(g11,g11) = 4
FEATURE [PartDesign::Pad] Pad003
  BaseFeature = -> Pocket006
  Length = 4
  Length2 = 100
  Profile = -> Sketch012
  Type = 0
FEATURE [Sketcher::SketchObject] Sketch013
  AttachmentOffset = pos=(0,0,-1.5) rot=(0,0,1;0rad)
  ExternalGeometry = -> [Pad003]
  MapMode = 5
  Placement = pos=(-30.3,0,0) rot=(0.57735,0.57735,0.57735;2.0944rad)
  Support = -> [Pad003]
  sketch-geometry (19):
    g0: LineSegment StartX=8.97421 StartY=10.9 StartZ=0 EndX=4.97421 EndY=10.9 EndZ=0
    g1: LineSegment StartX=4.97421 StartY=10.9 StartZ=0 EndX=4.97421 EndY=10.9 EndZ=0
    g2-g7: Circle [constr] x6 (B-spline internal-alignment scaffolding for g8; pole/knot coordinates omitted)
    g8: BSplineCurve PolesCount=6 KnotsCount=4 Degree=3 IsPeriodic=0
    g9-g12: GeomPoint [constr] x4 (B-spline internal-alignment scaffolding for g8; pole/knot coordinates omitted)
    g13: LineSegment StartX=4.97421 StartY=10.9 StartZ=0 EndX=4.97421 EndY=11.1578 EndZ=0
    g14: LineSegment [constr] StartX=7.97421 StartY=9.43769 StartZ=0 EndX=7.97421 EndY=9.43769 EndZ=0
    g15: LineSegment StartX=-4.62579 StartY=10.3 StartZ=0 EndX=-4.62579 EndY=10.2 EndZ=0
    g16: BSplineCurve PolesCount=6 KnotsCount=4 Degree=3 IsPeriodic=0
    g17: LineSegment StartX=-4.62579 StartY=10.2 StartZ=0 EndX=-1.62579 EndY=10.2 EndZ=0
    g18: LineSegment StartX=-1.62579 StartY=10.2 StartZ=0 EndX=-1.62579 EndY=11.1578 EndZ=0
  constraints (16):
    c: Coincident(g-5,g0)
    c: Coincident(g0,g-5)
    c: Coincident(g0,g1)
    c: Coincident(g1,g-4)
    c: Coincident(g2,g0)
    c: Radius(g2) = 0.02
    c: Equal(g2, g3-g7) x5
    c: PointOnObject(g7,g-4)
    c: InternalAlignment(g2-g7 -> g8) x6
    c: InternalAlignment(g9-g12 -> g8) x4
    c: Coincident(g13,g1)
    c: Coincident(g13,g7)
    c: Vertical(g14)
    c: Symmetric(g-6,g-7,g14)
    c: Coincident(g15,g17)
    c: Coincident(g18,g17)
FEATURE [PartDesign::Fillet] Fillet001
  Base = -> Pad003 [Edge150,Edge180,Edge178,Edge158]
  BaseFeature = -> Pad003
  Radius = 2
FEATURE [PartDesign::Pocket] Pocket007
  BaseFeature = -> Fillet001
  Length = 2.5
  Length2 = 100
  Profile = -> Sketch013
  Type = 0
FEATURE [PartDesign::Fillet] Fillet002
  Base = -> Pocket007 [Edge336,Edge337,Edge261,Edge260]
  BaseFeature = -> Pocket007
  Radius = 1
FEATURE [PartDesign::Fillet] Fillet003
  Base = -> Fillet002 [Edge385,Edge223]
  BaseFeature = -> Fillet002
  Radius = 0.2
FEATURE [PartDesign::Fillet] Fillet004
  Base = -> Fillet003 [Edge230,Edge196,Edge190,Edge109]
  BaseFeature = -> Fillet003
  Radius = 0.1
FEATURE [Sketcher::SketchObject] Sketch014
  ExternalGeometry = -> [Fillet004]
  MapMode = 5
  Placement = pos=(0,-17.3,0) rot=(1,0,0;1.5708rad)
  Support = -> [Fillet004]
  sketch-geometry (6):
    g0: LineSegment StartX=-26.0242 StartY=12 StartZ=0 EndX=-14.2242 EndY=12 EndZ=0
    g1: LineSegment StartX=-14.2242 StartY=12 StartZ=0 EndX=-14.2242 EndY=9.7 EndZ=0
    g2: LineSegment StartX=-14.2242 StartY=9.7 StartZ=0 EndX=-15.6543 EndY=8.5 EndZ=0
    g3: LineSegment StartX=-15.6543 StartY=8.5 StartZ=0 EndX=-24.5941 EndY=8.5 EndZ=0
    g4: LineSegment StartX=-24.5941 StartY=8.5 StartZ=0 EndX=-26.0242 EndY=9.7 EndZ=0
    g5: LineSegment StartX=-26.0242 StartY=9.7 StartZ=0 EndX=-26.0242 EndY=12 EndZ=0
  constraints (12):
    c: Coincident(g0,g-8)
    c: Coincident(g0,g-4)
    c: Coincident(g1,g0)
    c: Coincident(g1,g-5)
    c: Coincident(g2,g1)
    c: Coincident(g2,g-6)
    c: Coincident(g3,g2)
    c: Coincident(g3,g-7)
    c: Coincident(g4,g3)
    c: Coincident(g4,g-8)
    c: Coincident(g5,g4)
    c: Coincident(g5,g0)
FEATURE [PartDesign::Pad] Pad004
  BaseFeature = -> Fillet004
  Length = 1.5
  Length2 = 100
  Profile = -> Sketch014
  Reversed = true
  Type = 0
FEATURE [Sketcher::SketchObject] Sketch015
  ExternalGeometry = -> [Pad004]
  MapMode = 5
  Placement = pos=(0,-17.3,0) rot=(1,0,0;1.5708rad)
  Support = -> [Pad004]
  sketch-geometry (6):
    g0: LineSegment StartX=4.8858 StartY=12 StartZ=0 EndX=12.8858 EndY=12 EndZ=0
    g1: LineSegment StartX=12.8858 StartY=12 StartZ=0 EndX=12.8858 EndY=9.28 EndZ=0
    g2: LineSegment StartX=12.8858 StartY=9.28 StartZ=0 EndX=11.8858 EndY=8.28 EndZ=0
    g3: LineSegment StartX=11.8858 StartY=8.28 StartZ=0 EndX=5.8858 EndY=8.28 EndZ=0
    g4: LineSegment StartX=5.8858 StartY=8.28 StartZ=0 EndX=4.8858 EndY=9.28 EndZ=0
    g5: LineSegment StartX=4.8858 StartY=9.28 StartZ=0 EndX=4.8858 EndY=12 EndZ=0
  constraints (12):
    c: Coincident(g0,g-8)
    c: Coincident(g0,g-4)
    c: Coincident(g1,g0)
    c: Coincident(g1,g-5)
    c: Coincident(g2,g1)
    c: Coincident(g2,g-6)
    c: Coincident(g3,g2)
    c: Coincident(g3,g-7)
    c: Coincident(g4,g3)
    c: Coincident(g4,g-8)
    c: Coincident(g5,g4)
    c: Coincident(g5,g0)
FEATURE [PartDesign::Pad] Pad005
  BaseFeature = -> Pad004
  Length = 1
  Length2 = 100
  Profile = -> Sketch015
  Reversed = true
  Type = 0
FEATURE [PartDesign::Body] Body
  Group = -> [Sketch,Sketch001,Pad,Sketch002,Pocket,Sketch003,Pad001,Sketch004,Pad002,Sketch005,Pocket002,Sketch006,Pocket003,Chamfer,Sketch007,Hole,Sketch008,Pocket004,Sketch009,Hole001,Sketch010,Pocket005,Fillet,Sketch011,Pocket006,Sketch012,Pad003,Fillet001,Sketch013,Pocket007,Fillet002,Fillet003,Fillet004,Sketch014,Pad004,Sketch015,Pad005]
  Origin = -> Origin
  Tip = -> Pad005
FEATURE [Mesh::Feature] Mesh  label="Pad005 (Meshed)"
